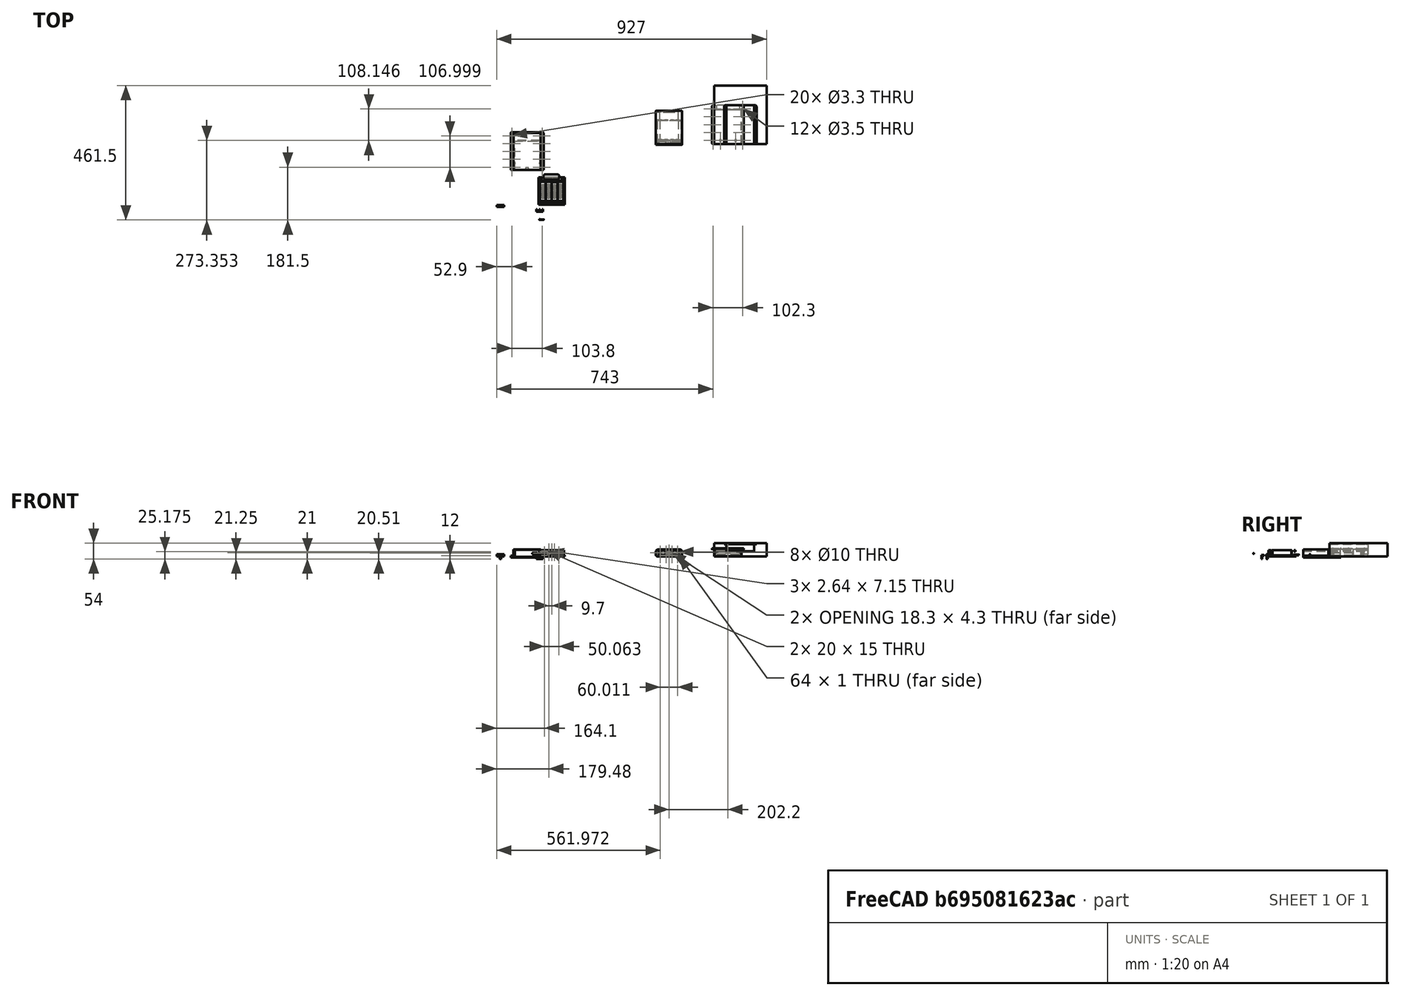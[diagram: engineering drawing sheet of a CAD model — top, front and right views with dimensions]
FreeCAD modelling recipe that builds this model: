
FCSTD DOCUMENT  (FreeCAD 0.21R33771 (Git))
Label: Battery V2
License: All rights reserved
LicenseURL: http://en.wikipedia.org/wiki/All_rights_reserved
objects: Sketcher::SketchObject×80, Part::Extrusion×28, PartDesign::Pocket×22, PartDesign::Fillet×19, App::Part×15, PartDesign::Pad×14, PartDesign::Body×13, PartDesign::Hole×13, App::MeasureDistance×12, Part::Feature×10, PartDesign::FeatureBase×10
note: 277 computed .brp shape members not serialized (recipe doc carries the construction recipe); baked Part::Feature solids carry a one-line shape summary decoded from their .brp

FEATURE [PartDesign::Body] BaseFeature010Body
  Origin = -> Origin117
FEATURE [PartDesign::Body] Body007  label="CELL MOUNT BODY"
  Origin = -> Origin098
FEATURE [PartDesign::Body] Body008  label="BACK BODY"
  Origin = -> Origin100
FEATURE [PartDesign::Body] Body011  label="HANDLE FASTEN PIN BODY"
  Origin = -> Origin106
FEATURE [App::MeasureDistance] Distance019  label="Distance: 3.33780 mm"
  Distance = 3.3378
  P1 = (43.5,-109.3,19.3861)
  P2 = (43.16,-112.62,19.44)
FEATURE [App::MeasureDistance] Distance020  label="Distance: 94.93000 mm"
  Distance = 94.93
  P1 = (84.2,-109.301,22.88)
  P2 = (84.2,-14.3705,22.88)
FEATURE [App::MeasureDistance] Distance021  label="Distance: 84.03434 mm"
  Distance = 84.0343
  P1 = (0.165655,-109.301,22.88)
  P2 = (84.2,-109.301,22.88)
FEATURE [App::MeasureDistance] Distance022  label="Distance: 22.78329 mm"
  Distance = 22.7833
  P1 = (0,-14.3705,22.7833)
  P2 = (0,-14.4,0)
FEATURE [App::MeasureDistance] Distance023  label="Distance: 10.06841 mm"
  Distance = 10.0684
  P1 = (82.0192,-16.37,21.3)
  P2 = (82.2,-26.4368,21.3)
FEATURE [App::MeasureDistance] Distance024  label="Distance: 7.48747 mm"
  Distance = 7.48747
  P1 = (82.0952,-107.281,21.3)
  P2 = (82.1396,-99.794,21.3)
FEATURE [App::MeasureDistance] Distance025  label="Distance: 1.03116 mm"
  Distance = 1.03116
  P1 = (82.2,-95.6714,11.6529)
  P2 = (82.1272,-96.7,11.65)
FEATURE [App::MeasureDistance] Distance026  label="Distance: 0.98878 mm"
  Distance = 0.988782
  P1 = (62.8884,-97.788,21.3)
  P2 = (61.9,-97.7591,21.3)
FEATURE [App::MeasureDistance] Distance027  label="Distance: 3.00017 mm"
  Distance = 3.00017
  P1 = (0,-109.3,3.96765)
  P2 = (-3,-109.3,3.93616)
FEATURE [App::MeasureDistance] Distance028  label="Distance: 90.20000 mm"
  Distance = 90.2
  P1 = (-3,-109.3,0)
  P2 = (87.2,-109.302,0)
FEATURE [App::MeasureDistance] Distance029  label="Distance: 94.80000 mm"
  Distance = 94.8
  P1 = (89.5,2.74181e-07,-2.3)
  P2 = (-5.3,2.74181e-07,-2.3)
FEATURE [App::MeasureDistance] Distance030  label="Distance: 94.92901 mm"
  Distance = 94.929
  P1 = (0,-109.3,22.6426)
  P2 = (0,-14.3705,22.6545)
FEATURE [App::Part] Part027  label="Batt Measurements"
  Group = -> [Distance019,Distance020,Distance021,Distance022,Distance023,Distance024,Distance025,Distance026,Distance027,Distance028,Distance029,Distance030]
  Origin = -> Origin110
FEATURE [Part::Feature] Part__Feature318  label="cell 001"
  Placement = pos=(11.67,-30.7,11.73) rot=(1,0,0;1.5708rad)
  shape: bbox 19.48 x 65 x 19.48 mm, 202 faces (baked)
FEATURE [Part::Feature] Part__Feature319  label="cell 002"
  Placement = pos=(32.21,-30.56,12.09) rot=(1,0,0;1.5708rad)
  shape: bbox 19.48 x 65 x 19.48 mm, 202 faces (baked)
FEATURE [Part::Feature] Part__Feature320  label="cell 003"
  Placement = pos=(52.45,-30.79,11.7) rot=(1,0,0;1.5708rad)
  shape: bbox 19.48 x 65 x 19.48 mm, 202 faces (baked)
FEATURE [Part::Feature] Part__Feature321  label="cell 004"
  Placement = pos=(72.58,-30.46,11.13) rot=(1,0,0;1.5708rad)
  shape: bbox 19.48 x 65 x 19.48 mm, 202 faces (baked)
FEATURE [App::Part] Part022  label="Batt Cells"
  Group = -> [Part__Feature318,Part__Feature319,Part__Feature320,Part__Feature321]
  Origin = -> Origin099
FEATURE [Part::Feature] Part__Feature565  label="sleeve enclosure v2"
  Placement = pos=(-0.1,0,24.3) rot=(0,1,0;3.14159rad)
  shape: bbox 112.8 x 127 x 25.3 mm, 56 faces (baked)
FEATURE [Part::Feature] Part__Feature566  label="sleeve enclosure top plate"
  Placement = pos=(-143.1,1e-15,-1) rot=(0,1,0;3.14159rad)
  shape: bbox 112.8 x 130 x 3 mm, 32 faces (baked)
FEATURE [App::Part] Part043  label="Battery Sleeve"
  Group = -> [Part__Feature565,Part__Feature566]
  Origin = -> Origin199
  Placement = pos=(84,-140.1,-3.2) rot=(0,0,1;0rad)
FEATURE [Sketcher::SketchObject] Sketch080
  FullyConstrained = false
  MapMode = 5
  Support = -> [XY_Plane098]
  sketch-geometry (4):
    g0: LineSegment StartX=0 StartY=-99.794 StartZ=0 EndX=84.2 EndY=-99.794 EndZ=0
    g1: LineSegment StartX=84.2 StartY=-99.794 StartZ=0 EndX=84.2 EndY=-26.494 EndZ=0
    g2: LineSegment StartX=84.2 StartY=-26.494 StartZ=0 EndX=0 EndY=-26.494 EndZ=0
    g3: LineSegment StartX=0 StartY=-26.494 StartZ=0 EndX=0 EndY=-99.794 EndZ=0
  constraints (10):
    c: Coincident(g0,g1)
    c: Coincident(g1,g2)
    c: Coincident(g2,g3)
    c: Coincident(g3,g0)
    c: Horizontal(g0)
    c: Horizontal(g2)
    c: Vertical(g1)
    c: Vertical(g3)
    c: DistanceX(g2,g2) = 84.2
    c: DistanceY(g3,g3) = 73.3
FEATURE [Part::Extrusion] Extrude026  label="CELL MOUNT FLOOR"
  Base = -> Sketch080
  Dir = (0,0,1)
  DirMode = 2
  FaceMakerClass = Part::FaceMakerBullseye
  LengthFwd = 2
  LengthRev = 0
  Solid = true
  Symmetric = false
FEATURE [Sketcher::SketchObject] Sketch081
  FullyConstrained = false
  MapMode = 5
  Placement = pos=(0,0,2) rot=(0,0,1;0rad)
  Support = -> [Extrude026]
  sketch-geometry (12):
    g0: LineSegment StartX=0 StartY=-26.494 StartZ=0 EndX=84.2 EndY=-26.494 EndZ=0
    g1: LineSegment StartX=84.2 StartY=-26.494 StartZ=0 EndX=84.2 EndY=-99.794 EndZ=0
    g2: LineSegment StartX=84.2 StartY=-99.794 StartZ=0 EndX=0 EndY=-99.794 EndZ=0
    g3: LineSegment StartX=0 StartY=-99.794 StartZ=0 EndX=0 EndY=-26.494 EndZ=0
    g4: LineSegment StartX=84.2 StartY=-99.794 StartZ=0 EndX=84.2 EndY=-97.79 EndZ=0
    g5: LineSegment StartX=84.2 StartY=-97.79 StartZ=0 EndX=82.2 EndY=-97.79 EndZ=0
    g6: LineSegment StartX=0 StartY=-26.494 StartZ=0 EndX=0 EndY=-28.49 EndZ=0
    g7: LineSegment StartX=0 StartY=-28.49 StartZ=0 EndX=2 EndY=-28.49 EndZ=0
    g8: LineSegment StartX=2 StartY=-28.49 StartZ=0 EndX=82.2 EndY=-28.49 EndZ=0
    g9: LineSegment StartX=82.2 StartY=-28.49 StartZ=0 EndX=82.2 EndY=-97.79 EndZ=0
    g10: LineSegment StartX=82.2 StartY=-97.79 StartZ=0 EndX=2 EndY=-97.79 EndZ=0
    g11: LineSegment StartX=2 StartY=-97.79 StartZ=0 EndX=2 EndY=-28.49 EndZ=0
  constraints (31):
    c: Coincident(g0,g1)
    c: Coincident(g1,g2)
    c: Coincident(g2,g3)
    c: Coincident(g3,g0)
    c: Horizontal(g0)
    c: Horizontal(g2)
    c: Vertical(g1)
    c: Vertical(g3)
    c: PointOnObject(g0,g-2)
    c: DistanceX(g2,g2) = 84.2
    c: DistanceY(g1,g1) = 73.3
    c: Coincident(g4,g1)
    c: PointOnObject(g4,g1)
    c: Coincident(g5,g4)
    c: Horizontal(g5)
    c: Coincident(g6,g0)
    c: PointOnObject(g6,g3)
    c: Coincident(g7,g6)
    c: Horizontal(g7)
    c: Coincident(g8,g9)
    c: Coincident(g9,g10)
    c: Coincident(g10,g11)
    c: Coincident(g11,g8)
    c: Horizontal(g8)
    c: Horizontal(g10)
    c: Vertical(g9)
    c: Vertical(g11)
    c: Coincident(g8,g7)
    c: Coincident(g9,g5)
    c: DistanceX(g8,g8) = 80.2
    c: DistanceY(g9,g9) = 69.3
FEATURE [Part::Extrusion] Extrude027  label="CELL MOUNT EXT WALLS"
  Base = -> Sketch081
  Dir = (0,0,1)
  DirMode = 2
  FaceMakerClass = Part::FaceMakerBullseye
  LengthFwd = 19.3
  LengthRev = 0
  Solid = true
  Symmetric = false
FEATURE [PartDesign::FeatureBase] BaseFeature012
  BaseFeature = -> Extrude027
FEATURE [Sketcher::SketchObject] Sketch082
  FullyConstrained = false
  MapMode = 5
  Placement = pos=(0,0,2) rot=(0,0,1;0rad)
  Support = -> [Extrude026]
  sketch-geometry (15):
    g0: LineSegment StartX=22.2999 StartY=-28.6 StartZ=0 EndX=41.5999 EndY=-28.6 EndZ=0
    g1: LineSegment StartX=21.2995 StartY=-28.49 StartZ=0 EndX=22.2995 EndY=-28.49 EndZ=0
    g2: LineSegment StartX=22.2995 StartY=-28.49 StartZ=0 EndX=22.2995 EndY=-97.8 EndZ=0
    g3: LineSegment StartX=22.2995 StartY=-97.8 StartZ=0 EndX=21.2995 EndY=-97.8 EndZ=0
    g4: LineSegment StartX=21.2995 StartY=-97.8 StartZ=0 EndX=21.2995 EndY=-28.49 EndZ=0
    g5: LineSegment StartX=41.6 StartY=-28.49 StartZ=0 EndX=42.6 EndY=-28.49 EndZ=0
    g6: LineSegment StartX=42.6 StartY=-28.49 StartZ=0 EndX=42.6 EndY=-97.79 EndZ=0
    g7: LineSegment StartX=42.6 StartY=-97.79 StartZ=0 EndX=41.6 EndY=-97.79 EndZ=0
    g8: LineSegment StartX=41.6 StartY=-97.79 StartZ=0 EndX=41.6 EndY=-28.49 EndZ=0
    g9: LineSegment StartX=42.6 StartY=-28.6021 StartZ=0 EndX=61.9 EndY=-28.6021 EndZ=0
    g10: LineSegment StartX=61.9 StartY=-28.49 StartZ=0 EndX=62.9 EndY=-28.49 EndZ=0
    g11: LineSegment StartX=62.9 StartY=-28.49 StartZ=0 EndX=62.9 EndY=-97.8 EndZ=0
    g12: LineSegment StartX=62.9 StartY=-97.8 StartZ=0 EndX=61.9 EndY=-97.8 EndZ=0
    g13: LineSegment StartX=61.9 StartY=-97.8 StartZ=0 EndX=61.9 EndY=-28.49 EndZ=0
    g14: LineSegment StartX=62.9 StartY=-28.601 StartZ=0 EndX=82.2 EndY=-28.601 EndZ=0
  constraints (38):
    c: Horizontal(g0)
    c: Coincident(g1,g2)
    c: Coincident(g2,g3)
    c: Coincident(g3,g4)
    c: Coincident(g4,g1)
    c: Horizontal(g1)
    c: Horizontal(g3)
    c: Vertical(g2)
    c: Vertical(g4)
    c: Coincident(g5,g6)
    c: Coincident(g6,g7)
    c: Coincident(g7,g8)
    c: Coincident(g8,g5)
    c: Horizontal(g5)
    c: Horizontal(g7)
    c: Vertical(g6)
    c: Vertical(g8)
    c: PointOnObject(g9,g6)
    c: Horizontal(g9)
    c: Coincident(g10,g11)
    c: Coincident(g11,g12)
    c: Coincident(g12,g13)
    c: Coincident(g13,g10)
    c: Horizontal(g10)
    c: Horizontal(g12)
    c: Vertical(g11)
    c: Vertical(g13)
    c: PointOnObject(g14,g11)
    c: Horizontal(g14)
    c: DistanceY(g4,g4) = 69.31
    c: DistanceY(g8,g8) = 69.3
    c: DistanceY(g13,g13) = 69.31
    c: DistanceX(g1,g1) = 1
    c: DistanceX(g0,g0) = 19.3
    c: DistanceX(g9,g9) = 19.3
    c: DistanceX(g5,g5) = 1
    c: DistanceX(g10,g10) = 1
    c: DistanceX(g14,g14) = 19.3
FEATURE [Part::Extrusion] Extrude028  label="CELL DIVIDER WALLS"
  Base = -> Sketch082
  Dir = (0,0,1)
  DirMode = 2
  FaceMakerClass = Part::FaceMakerBullseye
  LengthFwd = 19.3
  LengthRev = 0
  Solid = true
  Symmetric = false
FEATURE [Sketcher::SketchObject] Sketch083
  FullyConstrained = false
  MapMode = 5
  Placement = pos=(0,0,2) rot=(0,0,1;0rad)
  Support = -> [Extrude026]
  sketch-geometry (66):
    g0: LineSegment StartX=2.1 StartY=-28.49 StartZ=0 EndX=2.1 EndY=-29.49 EndZ=0
    g1: LineSegment StartX=2 StartY=-29.5 StartZ=0 EndX=6.5 EndY=-29.5 EndZ=0
    g2: LineSegment StartX=6.5 StartY=-29.5 StartZ=0 EndX=6.5 EndY=-30.5 EndZ=0
    g3: LineSegment StartX=6.5 StartY=-30.5 StartZ=0 EndX=2 EndY=-30.5 EndZ=0
    g4: LineSegment StartX=2 StartY=-30.5 StartZ=0 EndX=2 EndY=-29.5 EndZ=0
    g5: LineSegment StartX=21.3 StartY=-29.49 StartZ=0 EndX=16.8 EndY=-29.49 EndZ=0
    g6: LineSegment StartX=16.8 StartY=-29.49 StartZ=0 EndX=16.8 EndY=-30.49 EndZ=0
    g7: LineSegment StartX=16.8 StartY=-30.49 StartZ=0 EndX=21.3 EndY=-30.49 EndZ=0
    g8: LineSegment StartX=21.3 StartY=-30.49 StartZ=0 EndX=21.3 EndY=-29.49 EndZ=0
    g9: LineSegment StartX=22.3 StartY=-30.49 StartZ=0 EndX=26.8 EndY=-30.49 EndZ=0
    g10: LineSegment StartX=26.8 StartY=-30.49 StartZ=0 EndX=26.8 EndY=-29.49 EndZ=0
    g11: LineSegment StartX=26.8 StartY=-29.49 StartZ=0 EndX=22.3 EndY=-29.49 EndZ=0
    g12: LineSegment StartX=22.3 StartY=-29.49 StartZ=0 EndX=22.3 EndY=-30.49 EndZ=0
    g13: LineSegment StartX=41.6 StartY=-29.5 StartZ=0 EndX=37.1 EndY=-29.5 EndZ=0
    g14: LineSegment StartX=37.1 StartY=-29.5 StartZ=0 EndX=37.1 EndY=-30.5 EndZ=0
    g15: LineSegment StartX=37.1 StartY=-30.5 StartZ=0 EndX=41.6 EndY=-30.5 EndZ=0
    g16: LineSegment StartX=41.6 StartY=-30.5 StartZ=0 EndX=41.6 EndY=-29.5 EndZ=0
    g17: LineSegment StartX=42.6 StartY=-29.5 StartZ=0 EndX=47.1 EndY=-29.5 EndZ=0
    g18: LineSegment StartX=47.1 StartY=-29.5 StartZ=0 EndX=47.1 EndY=-30.5 EndZ=0
    g19: LineSegment StartX=47.1 StartY=-30.5 StartZ=0 EndX=42.6 EndY=-30.5 EndZ=0
    g20: LineSegment StartX=42.6 StartY=-30.5 StartZ=0 EndX=42.6 EndY=-29.5 EndZ=0
    g21: LineSegment StartX=61.9 StartY=-29.5 StartZ=0 EndX=57.4 EndY=-29.5 EndZ=0
    g22: LineSegment StartX=57.4 StartY=-29.5 StartZ=0 EndX=57.4 EndY=-30.5 EndZ=0
    g23: LineSegment StartX=57.4 StartY=-30.5 StartZ=0 EndX=61.9 EndY=-30.5 EndZ=0
    g24: LineSegment StartX=61.9 StartY=-30.5 StartZ=0 EndX=61.9 EndY=-29.5 EndZ=0
    g25: LineSegment StartX=62.9 StartY=-29.5 StartZ=0 EndX=67.4 EndY=-29.5 EndZ=0
    g26: LineSegment StartX=67.4 StartY=-29.5 StartZ=0 EndX=67.4 EndY=-30.5 EndZ=0
    g27: LineSegment StartX=67.4 StartY=-30.5 StartZ=0 EndX=62.9 EndY=-30.5 EndZ=0
    g28: LineSegment StartX=62.9 StartY=-30.5 StartZ=0 EndX=62.9 EndY=-29.5 EndZ=0
    g29: LineSegment StartX=82.2 StartY=-29.5 StartZ=0 EndX=77.7 EndY=-29.5 EndZ=0
    g30: LineSegment StartX=77.7 StartY=-29.5 StartZ=0 EndX=77.7 EndY=-30.5 EndZ=0
    g31: LineSegment StartX=77.7 StartY=-30.5 StartZ=0 EndX=82.2 EndY=-30.5 EndZ=0
    g32: LineSegment StartX=82.2 StartY=-30.5 StartZ=0 EndX=82.2 EndY=-29.5 EndZ=0
    g33: LineSegment StartX=2.1 StartY=-97.79 StartZ=0 EndX=2.1 EndY=-96.7 EndZ=0
    g34: LineSegment StartX=2 StartY=-96.7 StartZ=0 EndX=6.5 EndY=-96.7 EndZ=0
    g35: LineSegment StartX=6.5 StartY=-96.7 StartZ=0 EndX=6.5 EndY=-95.7 EndZ=0
    g36: LineSegment StartX=6.5 StartY=-95.7 StartZ=0 EndX=2 EndY=-95.7 EndZ=0
    g37: LineSegment StartX=2 StartY=-95.7 StartZ=0 EndX=2 EndY=-96.7 EndZ=0
    g38: LineSegment StartX=21.3 StartY=-95.7 StartZ=0 EndX=16.8 EndY=-95.7 EndZ=0
    g39: LineSegment StartX=16.8 StartY=-95.7 StartZ=0 EndX=16.8 EndY=-96.7 EndZ=0
    g40: LineSegment StartX=16.8 StartY=-96.7 StartZ=0 EndX=21.3 EndY=-96.7 EndZ=0
    g41: LineSegment StartX=21.3 StartY=-96.7 StartZ=0 EndX=21.3 EndY=-95.7 EndZ=0
    g42: LineSegment StartX=22.3 StartY=-96.7 StartZ=0 EndX=26.8 EndY=-96.7 EndZ=0
    g43: LineSegment StartX=26.8 StartY=-96.7 StartZ=0 EndX=26.8 EndY=-95.7 EndZ=0
    g44: LineSegment StartX=26.8 StartY=-95.7 StartZ=0 EndX=22.3 EndY=-95.7 EndZ=0
    g45: LineSegment StartX=22.3 StartY=-95.7 StartZ=0 EndX=22.3 EndY=-96.7 EndZ=0
    g46: LineSegment StartX=41.6 StartY=-95.7 StartZ=0 EndX=37.1 EndY=-95.7 EndZ=0
    g47: LineSegment StartX=37.1 StartY=-95.7 StartZ=0 EndX=37.1 EndY=-96.7 EndZ=0
    g48: LineSegment StartX=37.1 StartY=-96.7 StartZ=0 EndX=41.6 EndY=-96.7 EndZ=0
    g49: LineSegment StartX=41.6 StartY=-96.7 StartZ=0 EndX=41.6 EndY=-95.7 EndZ=0
    g50: LineSegment StartX=42.6 StartY=-96.7 StartZ=0 EndX=47.1 EndY=-96.7 EndZ=0
    g51: LineSegment StartX=47.1 StartY=-96.7 StartZ=0 EndX=47.1 EndY=-95.7 EndZ=0
    g52: LineSegment StartX=47.1 StartY=-95.7 StartZ=0 EndX=42.6 EndY=-95.7 EndZ=0
    g53: LineSegment StartX=42.6 StartY=-95.7 StartZ=0 EndX=42.6 EndY=-96.7 EndZ=0
    g54: LineSegment StartX=61.9 StartY=-95.7 StartZ=0 EndX=57.4 EndY=-95.7 EndZ=0
    g55: LineSegment StartX=57.4 StartY=-95.7 StartZ=0 EndX=57.4 EndY=-96.7 EndZ=0
    g56: LineSegment StartX=57.4 StartY=-96.7 StartZ=0 EndX=61.9 EndY=-96.7 EndZ=0
    g57: LineSegment StartX=61.9 StartY=-96.7 StartZ=0 EndX=61.9 EndY=-95.7 EndZ=0
    g58: LineSegment StartX=62.9 StartY=-95.7 StartZ=0 EndX=67.4 EndY=-95.7 EndZ=0
    g59: LineSegment StartX=67.4 StartY=-95.7 StartZ=0 EndX=67.4 EndY=-96.7 EndZ=0
    g60: LineSegment StartX=67.4 StartY=-96.7 StartZ=0 EndX=62.9 EndY=-96.7 EndZ=0
    g61: LineSegment StartX=62.9 StartY=-96.7 StartZ=0 EndX=62.9 EndY=-95.7 EndZ=0
    g62: LineSegment StartX=82.2 StartY=-95.7 StartZ=0 EndX=77.7 EndY=-95.7 EndZ=0
    g63: LineSegment StartX=77.7 StartY=-95.7 StartZ=0 EndX=77.7 EndY=-96.7 EndZ=0
    g64: LineSegment StartX=77.7 StartY=-96.7 StartZ=0 EndX=82.2 EndY=-96.7 EndZ=0
    g65: LineSegment StartX=82.2 StartY=-96.7 StartZ=0 EndX=82.2 EndY=-95.7 EndZ=0
  constraints (162):
    c: Vertical(g0)
    c: Coincident(g1,g2)
    c: Coincident(g2,g3)
    c: Coincident(g3,g4)
    c: Coincident(g4,g1)
    c: Horizontal(g1)
    c: Horizontal(g3)
    c: Vertical(g2)
    c: Vertical(g4)
    c: Coincident(g5,g6)
    c: Coincident(g6,g7)
    c: Coincident(g7,g8)
    c: Coincident(g8,g5)
    c: Horizontal(g5)
    c: Horizontal(g7)
    c: Vertical(g6)
    c: Vertical(g8)
    c: DistanceX(g1,g1) = 4.5
    c: DistanceX(g5,g5) = 4.5
    c: DistanceY(g2,g2) = 1
    c: DistanceY(g6,g6) = 1
    c: Coincident(g9,g10)
    c: Coincident(g10,g11)
    c: Coincident(g11,g12)
    c: Coincident(g12,g9)
    c: Horizontal(g9)
    c: Horizontal(g11)
    c: Vertical(g10)
    c: Vertical(g12)
    c: Coincident(g13,g14)
    c: Coincident(g14,g15)
    c: Coincident(g15,g16)
    c: Coincident(g16,g13)
    c: Horizontal(g13)
    c: Horizontal(g15)
    c: Vertical(g14)
    c: Vertical(g16)
    c: DistanceX(g13,g13) = 4.5
    c: DistanceX(g11,g11) = 4.5
    c: DistanceY(g10,g10) = 1
    c: DistanceY(g14,g14) = 1
    c: Coincident(g17,g18)
    c: Coincident(g18,g19)
    c: Coincident(g19,g20)
    c: Coincident(g20,g17)
    c: Horizontal(g17)
    c: Horizontal(g19)
    c: Vertical(g18)
    c: Vertical(g20)
    c: Coincident(g21,g22)
    c: Coincident(g22,g23)
    c: Coincident(g23,g24)
    c: Coincident(g24,g21)
    c: Horizontal(g21)
    c: Horizontal(g23)
    c: Vertical(g22)
    c: Vertical(g24)
    c: DistanceX(g17,g17) = 4.5
    c: DistanceY(g18,g18) = 1
    c: DistanceX(g21,g21) = 4.5
    c: DistanceY(g22,g22) = 1
    c: Coincident(g25,g26)
    c: Coincident(g26,g27)
    c: Coincident(g27,g28)
    c: Coincident(g28,g25)
    c: Horizontal(g25)
    c: Horizontal(g27)
    c: Vertical(g26)
    c: Vertical(g28)
    c: Coincident(g29,g30)
    c: Coincident(g30,g31)
    c: Coincident(g31,g32)
    c: Coincident(g32,g29)
    c: Horizontal(g29)
    c: Horizontal(g31)
    c: Vertical(g30)
    c: Vertical(g32)
    c: DistanceX(g29,g29) = 4.5
    c: DistanceX(g25,g25) = 4.5
    c: DistanceY(g26,g26) = 1
    c: DistanceY(g30,g30) = 1
    c: Vertical(g33)
    c: Coincident(g34,g35)
    c: Coincident(g35,g36)
    c: Coincident(g36,g37)
    c: Coincident(g37,g34)
    c: Horizontal(g34)
    c: Horizontal(g36)
    c: Vertical(g35)
    c: Vertical(g37)
    c: Coincident(g38,g39)
    c: Coincident(g39,g40)
    c: Coincident(g40,g41)
    c: Coincident(g41,g38)
    c: Horizontal(g38)
    c: Horizontal(g40)
    c: Vertical(g39)
    c: Vertical(g41)
    c: DistanceY(g39,g39) = 1
    c: DistanceY(g35,g35) = 1
    c: DistanceX(g36,g36) = 4.5
    c: DistanceX(g38,g38) = 4.5
    c: Coincident(g42,g43)
    c: Coincident(g43,g44)
    c: Coincident(g44,g45)
    c: Coincident(g45,g42)
    c: Horizontal(g42)
    c: Horizontal(g44)
    c: Vertical(g43)
    c: Vertical(g45)
    c: Coincident(g46,g47)
    c: Coincident(g47,g48)
    c: Coincident(g48,g49)
    c: Coincident(g49,g46)
    c: Horizontal(g46)
    c: Horizontal(g48)
    c: Vertical(g47)
    c: Vertical(g49)
    c: DistanceX(g46,g46) = 4.5
    c: DistanceX(g44,g44) = 4.5
    c: DistanceY(g43,g43) = 1
    c: DistanceY(g47,g47) = 1
    c: Coincident(g50,g51)
    c: Coincident(g51,g52)
    c: Coincident(g52,g53)
    c: Coincident(g53,g50)
    c: Horizontal(g50)
    c: Horizontal(g52)
    c: Vertical(g51)
    c: Vertical(g53)
    c: DistanceY(g51,g51) = 1
    c: DistanceX(g52,g52) = 4.5
    c: Coincident(g54,g55)
    c: Coincident(g55,g56)
    c: Coincident(g56,g57)
    c: Coincident(g57,g54)
    c: Horizontal(g54)
    c: Horizontal(g56)
    c: Vertical(g55)
    c: Vertical(g57)
    c: DistanceX(g54,g54) = 4.5
    c: DistanceY(g55,g55) = 1
    c: Coincident(g58,g59)
    c: Coincident(g59,g60)
    c: Coincident(g60,g61)
    c: Coincident(g61,g58)
    c: Horizontal(g58)
    c: Horizontal(g60)
    c: Vertical(g59)
    c: Vertical(g61)
    c: DistanceY(g59,g59) = 1
    c: DistanceX(g60,g60) = 4.5
    c: Coincident(g62,g63)
    c: Coincident(g63,g64)
    c: Coincident(g64,g65)
    c: Coincident(g65,g62)
    c: Horizontal(g62)
    c: Horizontal(g64)
    c: Vertical(g63)
    c: Vertical(g65)
    c: DistanceY(g63,g63) = 1
    c: DistanceX(g62,g62) = 4.5
FEATURE [Part::Extrusion] Extrude029  label="CELL ENDS SPRING HOLDERS"
  Base = -> Sketch083
  Dir = (0,0,1)
  DirMode = 2
  FaceMakerClass = Part::FaceMakerBullseye
  LengthFwd = 9.65
  LengthRev = 0
  Solid = true
  Symmetric = false
FEATURE [Sketcher::SketchObject] Sketch084
  FullyConstrained = false
  MapMode = 5
  Support = -> [XY_Plane098]
  sketch-geometry (4):
    g0: LineSegment StartX=0 StartY=-26.49 StartZ=0 EndX=84.2 EndY=-26.49 EndZ=0
    g1: LineSegment StartX=84.2 StartY=-26.49 StartZ=0 EndX=84.2 EndY=-14.4 EndZ=0
    g2: LineSegment StartX=84.2 StartY=-14.4 StartZ=0 EndX=0 EndY=-14.4 EndZ=0
    g3: LineSegment StartX=0 StartY=-14.4 StartZ=0 EndX=0 EndY=-26.49 EndZ=0
  constraints (11):
    c: Coincident(g0,g1)
    c: Coincident(g1,g2)
    c: Coincident(g2,g3)
    c: Coincident(g3,g0)
    c: Horizontal(g0)
    c: Horizontal(g2)
    c: Vertical(g1)
    c: Vertical(g3)
    c: PointOnObject(g0,g-2)
    c: DistanceX(g2,g2) = 84.2
    c: DistanceY(g1,g1) = 12.09
FEATURE [Part::Extrusion] Extrude030  label="BACK FLOOR"
  Base = -> Sketch084
  Dir = (0,0,1)
  DirMode = 2
  FaceMakerClass = Part::FaceMakerBullseye
  LengthFwd = 2
  LengthRev = 0
  Solid = true
  Symmetric = false
FEATURE [Sketcher::SketchObject] Sketch085
  FullyConstrained = false
  MapMode = 5
  Placement = pos=(0,0,2) rot=(0,0,1;0rad)
  Support = -> [Extrude030]
  sketch-geometry (8):
    g0: LineSegment StartX=0 StartY=-26.4942 StartZ=0 EndX=84.2 EndY=-26.4942 EndZ=0
    g1: LineSegment StartX=84.2 StartY=-26.4942 StartZ=0 EndX=84.2 EndY=-14.4 EndZ=0
    g2: LineSegment StartX=84.2 StartY=-14.4 StartZ=0 EndX=0 EndY=-14.4 EndZ=0
    g3: LineSegment StartX=0 StartY=-14.4 StartZ=0 EndX=0 EndY=-26.4942 EndZ=0
    g4: LineSegment StartX=82.2 StartY=-26.4942 StartZ=0 EndX=2 EndY=-26.4942 EndZ=0
    g5: LineSegment StartX=2 StartY=-26.4942 StartZ=0 EndX=2 EndY=-16.37 EndZ=0
    g6: LineSegment StartX=2 StartY=-16.37 StartZ=0 EndX=82.2 EndY=-16.37 EndZ=0
    g7: LineSegment StartX=82.2 StartY=-16.37 StartZ=0 EndX=82.2 EndY=-26.4942 EndZ=0
  constraints (22):
    c: Coincident(g0,g1)
    c: Coincident(g1,g2)
    c: Coincident(g2,g3)
    c: Coincident(g3,g0)
    c: Horizontal(g0)
    c: Horizontal(g2)
    c: Vertical(g1)
    c: Vertical(g3)
    c: PointOnObject(g0,g-2)
    c: Coincident(g4,g5)
    c: Coincident(g5,g6)
    c: Coincident(g6,g7)
    c: Coincident(g7,g4)
    c: Horizontal(g4)
    c: Horizontal(g6)
    c: Vertical(g5)
    c: Vertical(g7)
    c: PointOnObject(g4,g0)
    c: DistanceX(g6,g6) = 80.2
    c: DistanceX(g2,g2) = 84.2
    c: DistanceY(g5,g5) = 10.1242
    c: DistanceY(g3,g3) = 12.0942
FEATURE [Part::Extrusion] Extrude005  label="Extrude062"
  Base = -> Sketch085
  Dir = (0,0,1)
  DirMode = 2
  FaceMakerClass = Part::FaceMakerBullseye
  LengthFwd = 19.3
  LengthRev = 0
  Solid = true
  Symmetric = false
FEATURE [PartDesign::FeatureBase] BaseFeature006
  BaseFeature = -> Extrude005
FEATURE [Sketcher::SketchObject] Sketch086
  FullyConstrained = false
  MapMode = 5
  Placement = pos=(0,-14.4,0) rot=(0,0.707107,0.707107;3.14159rad)
  Support = -> [BaseFeature006]
  sketch-geometry (4):
    g0: LineSegment StartX=-7 StartY=10 StartZ=0 EndX=-24.64 EndY=10 EndZ=0
    g1: LineSegment StartX=-24.64 StartY=10 StartZ=0 EndX=-24.64 EndY=14 EndZ=0
    g2: LineSegment StartX=-24.64 StartY=14 StartZ=0 EndX=-7 EndY=14 EndZ=0
    g3: LineSegment StartX=-7 StartY=14 StartZ=0 EndX=-7 EndY=10 EndZ=0
  constraints (10):
    c: Coincident(g0,g1)
    c: Coincident(g1,g2)
    c: Coincident(g2,g3)
    c: Coincident(g3,g0)
    c: Horizontal(g0)
    c: Horizontal(g2)
    c: Vertical(g1)
    c: Vertical(g3)
    c: DistanceX(g2,g2) = 17.64
    c: DistanceY(g1,g1) = 4
FEATURE [PartDesign::Pocket] Pocket017  label="BACK WALL"
  Direction = (0,-1,2e-16)
  Length = 2
  Length2 = 5
  Profile = -> Sketch086
  ReferenceAxis = -> Sketch086 [N_Axis]
  Type = 0
FEATURE [Sketcher::SketchObject] Sketch087
  FullyConstrained = false
  MapMode = 5
  Support = -> [XY_Plane102]
  sketch-geometry (4):
    g0: LineSegment StartX=-140 StartY=-110 StartZ=0 EndX=-128 EndY=-110 EndZ=0
    g1: LineSegment StartX=-128 StartY=-110 StartZ=0 EndX=-128 EndY=-117 EndZ=0
    g2: LineSegment StartX=-128 StartY=-117 StartZ=0 EndX=-140 EndY=-117 EndZ=0
    g3: LineSegment StartX=-140 StartY=-117 StartZ=0 EndX=-140 EndY=-110 EndZ=0
  constraints (10):
    c: Coincident(g0,g1)
    c: Coincident(g1,g2)
    c: Coincident(g2,g3)
    c: Coincident(g3,g0)
    c: Horizontal(g0)
    c: Horizontal(g2)
    c: Vertical(g1)
    c: Vertical(g3)
    c: DistanceX(g0,g0) = 12
    c: DistanceY(g3,g3) = 7
FEATURE [Part::Extrusion] Extrude007
  Base = -> Sketch087
  Dir = (0,0,1)
  DirMode = 2
  FaceMakerClass = Part::FaceMakerBullseye
  LengthFwd = 7
  LengthRev = 0
  Solid = true
  Symmetric = false
FEATURE [PartDesign::FeatureBase] BaseFeature007
  BaseFeature = -> Extrude007
FEATURE [Sketcher::SketchObject] Sketch012
  FullyConstrained = false
  MapMode = 5
  Placement = pos=(0,0,7) rot=(0,0,1;0rad)
  Support = -> [Extrude007]
  sketch-geometry (4):
    g0: LineSegment StartX=-139 StartY=-111 StartZ=0 EndX=-129 EndY=-111 EndZ=0
    g1: LineSegment StartX=-129 StartY=-111 StartZ=0 EndX=-129 EndY=-116 EndZ=0
    g2: LineSegment StartX=-129 StartY=-116 StartZ=0 EndX=-139 EndY=-116 EndZ=0
    g3: LineSegment StartX=-139 StartY=-116 StartZ=0 EndX=-139 EndY=-111 EndZ=0
  constraints (10):
    c: Coincident(g0,g1)
    c: Coincident(g1,g2)
    c: Coincident(g2,g3)
    c: Coincident(g3,g0)
    c: Horizontal(g0)
    c: Horizontal(g2)
    c: Vertical(g1)
    c: Vertical(g3)
    c: DistanceY(g3,g3) = 5
    c: DistanceX(g0,g0) = 10
FEATURE [Sketcher::SketchObject] Sketch088
  FullyConstrained = false
  MapMode = 5
  Placement = pos=(0,-117,0) rot=(1,0,0;1.5708rad)
  Support = -> [Extrude007]
  sketch-geometry (4):
    g0: LineSegment StartX=-135 StartY=2 StartZ=0 EndX=-133 EndY=2 EndZ=0
    g1: LineSegment StartX=-133 StartY=2 StartZ=0 EndX=-133 EndY=5 EndZ=0
    g2: LineSegment StartX=-133 StartY=5 StartZ=0 EndX=-135 EndY=5 EndZ=0
    g3: LineSegment StartX=-135 StartY=5 StartZ=0 EndX=-135 EndY=2 EndZ=0
  constraints (10):
    c: Coincident(g0,g1)
    c: Coincident(g1,g2)
    c: Coincident(g2,g3)
    c: Coincident(g3,g0)
    c: Horizontal(g0)
    c: Horizontal(g2)
    c: Vertical(g1)
    c: Vertical(g3)
    c: DistanceX(g2,g2) = 2
    c: DistanceY(g3,g3) = 3
FEATURE [PartDesign::Pocket] Pocket018
  Direction = (0,1,-2e-16)
  Length = 3.5
  Length2 = 5
  Profile = -> Sketch088
  ReferenceAxis = -> Sketch088 [N_Axis]
  Type = 0
FEATURE [PartDesign::FeatureBase] BaseFeature008
  BaseFeature = -> Pocket018
FEATURE [Sketcher::SketchObject] Sketch089
  FullyConstrained = false
  MapMode = 5
  Placement = pos=(-128,0,0) rot=(0.57735,0.57735,0.57735;2.0944rad)
  Support = -> [Pocket018]
  sketch-geometry (1):
    g0: Circle CenterX=-115.25 CenterY=3.5 CenterZ=0 NormalX=0 NormalY=0 NormalZ=1 AngleXU=0 Radius=0.75
  constraints (1):
    c: Diameter(g0) = 1.5
FEATURE [PartDesign::Hole] Hole018  label="MAIN LOCKING HANDLE MNT"
  CustomThreadClearance = 0
  Depth = 12
  DepthType = 0
  Diameter = 1.5
  DrillForDepth = false
  DrillPoint = 1
  DrillPointAngle = 118
  HoleCutCountersinkAngle = 90
  HoleCutCustomValues = false
  HoleCutDepth = 0
  HoleCutDiameter = 6.1
  HoleCutType = 0
  ModelThread = false
  Profile = -> Sketch089
  Tapered = false
  TaperedAngle = 90
  ThreadClass = 0
  ThreadDepth = 12
  ThreadDepthType = 0
  ThreadDirection = 0
  ThreadFit = 0
  ThreadSize = 0
  ThreadType = 0
  Threaded = false
  UseCustomThreadClearance = false
FEATURE [Sketcher::SketchObject] Sketch090
  FullyConstrained = false
  MapMode = 5
  Placement = pos=(0,0,0) rot=(0.57735,0.57735,0.57735;2.0944rad)
  Support = -> [YZ_Plane104]
  sketch-geometry (17):
    g0: LineSegment StartX=-128 StartY=5 StartZ=0 EndX=-130 EndY=5 EndZ=0
    g1: LineSegment StartX=-130 StartY=5 StartZ=0 EndX=-130.3 EndY=5 EndZ=0
    g2: LineSegment StartX=-130.3 StartY=5 StartZ=0 EndX=-133.3 EndY=5 EndZ=0
    g3: LineSegment StartX=-133.3 StartY=5 StartZ=0 EndX=-133.3 EndY=3 EndZ=0
    g4: LineSegment StartX=-133.3 StartY=3 StartZ=0 EndX=-131.8 EndY=3 EndZ=0
    g5: LineSegment StartX=-131.8 StartY=3 StartZ=0 EndX=-131.8 EndY=-7 EndZ=0
    g6: LineSegment StartX=-131.8 StartY=-7 StartZ=0 EndX=-133.3 EndY=-7 EndZ=0
    g7: LineSegment StartX=-133.3 StartY=-7 StartZ=0 EndX=-133.3 EndY=-9 EndZ=0
    g8: LineSegment StartX=-133.3 StartY=-9 StartZ=0 EndX=-130.3 EndY=-9 EndZ=0
    g9: LineSegment StartX=-128 StartY=5 StartZ=0 EndX=-127.7 EndY=5 EndZ=0
    g10: LineSegment StartX=-127.7 StartY=5 StartZ=0 EndX=-124.2 EndY=5 EndZ=0
    g11: LineSegment StartX=-124.2 StartY=5 StartZ=0 EndX=-124.2 EndY=2 EndZ=0
    g12: LineSegment StartX=-124.2 StartY=2 StartZ=0 EndX=-127.7 EndY=2 EndZ=0
    g13: LineSegment StartX=-127.7 StartY=2 StartZ=0 EndX=-128 EndY=2 EndZ=0
    g14: LineSegment StartX=-128 StartY=2 StartZ=0 EndX=-130 EndY=2 EndZ=0
    g15: LineSegment StartX=-130 StartY=2 StartZ=0 EndX=-130.3 EndY=2 EndZ=0
    g16: LineSegment StartX=-130.3 StartY=2 StartZ=0 EndX=-130.3 EndY=-9 EndZ=0
  constraints (49):
    c: Horizontal(g0)
    c: Coincident(g0,g1)
    c: Horizontal(g1)
    c: Coincident(g1,g2)
    c: Horizontal(g2)
    c: Coincident(g2,g3)
    c: Vertical(g3)
    c: Coincident(g3,g4)
    c: Horizontal(g4)
    c: Coincident(g4,g5)
    c: Vertical(g5)
    c: Coincident(g5,g6)
    c: Horizontal(g6)
    c: Coincident(g6,g7)
    c: Vertical(g7)
    c: Coincident(g7,g8)
    c: Horizontal(g8)
    c: DistanceY(g5,g5) = 10
    c: DistanceY(g3,g3) = 2
    c: DistanceX(g4,g4) = 1.5
    c: DistanceX(g2,g2) = 3
    c: DistanceX(g1,g1) = 0.3
    c: DistanceX(g0,g0) = 2
    c: DistanceX(g6,g6) = 1.5
    c: Coincident(g9,g0)
    c: Horizontal(g9)
    c: Coincident(g9,g10)
    c: Horizontal(g10)
    c: Coincident(g10,g11)
    c: Vertical(g11)
    c: Coincident(g11,g12)
    c: Horizontal(g12)
    c: Coincident(g12,g13)
    c: Horizontal(g13)
    c: Coincident(g13,g14)
    c: Horizontal(g14)
    c: Coincident(g15,g14)
    c: Horizontal(g15)
    c: Coincident(g15,g16)
    c: Coincident(g16,g8)
    c: Vertical(g16)
    c: DistanceY(g7,g7) = 2
    c: DistanceY(g16,g16) = 11
    c: DistanceX(g8,g8) = 3
    c: DistanceX(g15,g15) = 0.3
    c: DistanceX(g14,g14) = 2
    c: DistanceX(g13,g13) = 0.3
    c: DistanceX(g12,g12) = 3.5
    c: DistanceX(g10,g10) = 3.5
FEATURE [Part::Extrusion] Extrude041  label="Extrude071"
  Base = -> Sketch090
  Dir = (1,-1e-16,1e-16)
  DirMode = 2
  FaceMakerClass = Part::FaceMakerBullseye
  LengthFwd = 2
  LengthRev = 0
  Solid = true
  Symmetric = false
FEATURE [Sketcher::SketchObject] Sketch091
  FullyConstrained = false
  MapMode = 5
  Placement = pos=(0,0,0) rot=(0.57735,0.57735,0.57735;2.0944rad)
  Support = -> [YZ_Plane106]
  sketch-geometry (1):
    g0: Circle CenterX=-160 CenterY=10 CenterZ=0 NormalX=0 NormalY=0 NormalZ=1 AngleXU=0 Radius=1.5
  constraints (1):
    c: Diameter(g0) = 3
FEATURE [Part::Extrusion] Extrude011  label="PIN BASE"
  Base = -> Sketch091
  Dir = (1,-1e-16,1e-16)
  DirMode = 2
  FaceMakerClass = Part::FaceMakerBullseye
  LengthFwd = 1.5
  LengthRev = 0
  Solid = true
  Symmetric = false
FEATURE [Sketcher::SketchObject] Sketch092
  FullyConstrained = false
  MapMode = 5
  Placement = pos=(1.5,-3e-16,3e-16) rot=(0.57735,0.57735,0.57735;2.0944rad)
  Support = -> [Extrude011]
  sketch-geometry (1):
    g0: Circle CenterX=-160 CenterY=10 CenterZ=0 NormalX=0 NormalY=0 NormalZ=1 AngleXU=0 Radius=0.74
  constraints (1):
    c: Diameter(g0) = 1.48
FEATURE [Part::Extrusion] Extrude012  label="PIN LENGTH"
  Base = -> Sketch092
  Dir = (1,-2e-16,2e-16)
  DirMode = 2
  FaceMakerClass = Part::FaceMakerBullseye
  LengthFwd = 13.5
  LengthRev = 0
  Solid = true
  Symmetric = false
FEATURE [App::Part] Part025  label="handle to mechanism pin"
  Group = -> [Body011,Sketch091,Extrude011,Sketch092,Extrude012]
  Origin = -> Origin105
  Placement = pos=(34.67,54.77,7.74) rot=(0,0,1;0rad)
FEATURE [Sketcher::SketchObject] Sketch093
  FullyConstrained = false
  MapMode = 5
  Support = -> [XY_Plane107]
  sketch-geometry (4):
    g0: LineSegment StartX=0 StartY=-99.794 StartZ=0 EndX=84.2 EndY=-99.794 EndZ=0
    g1: LineSegment StartX=84.2 StartY=-99.794 StartZ=0 EndX=84.2 EndY=-109.304 EndZ=0
    g2: LineSegment StartX=84.2 StartY=-109.304 StartZ=0 EndX=0 EndY=-109.304 EndZ=0
    g3: LineSegment StartX=0 StartY=-109.304 StartZ=0 EndX=0 EndY=-99.794 EndZ=0
  constraints (11):
    c: Coincident(g0,g1)
    c: Coincident(g1,g2)
    c: Coincident(g2,g3)
    c: Coincident(g3,g0)
    c: Horizontal(g0)
    c: Horizontal(g2)
    c: Vertical(g1)
    c: Vertical(g3)
    c: PointOnObject(g0,g-2)
    c: DistanceX(g2,g2) = 84.2
    c: DistanceY(g1,g1) = 9.51
FEATURE [Part::Extrusion] Extrude031  label="Extrude063"
  Base = -> Sketch093
  Dir = (0,0,1)
  DirMode = 2
  FaceMakerClass = Part::FaceMakerBullseye
  LengthFwd = 2
  LengthRev = 0
  Solid = true
  Symmetric = false
FEATURE [PartDesign::FeatureBase] BaseFeature009  label="FRONT FLOOR"
  BaseFeature = -> Extrude031
FEATURE [Sketcher::SketchObject] Sketch094
  FullyConstrained = false
  MapMode = 5
  Placement = pos=(0,0,2) rot=(0,0,1;0rad)
  Support = -> [Extrude031]
  sketch-geometry (8):
    g0: LineSegment StartX=0 StartY=-99.8 StartZ=0 EndX=0 EndY=-109.3 EndZ=0
    g1: LineSegment StartX=0 StartY=-109.3 StartZ=0 EndX=84.2 EndY=-109.3 EndZ=0
    g2: LineSegment StartX=84.2 StartY=-109.3 StartZ=0 EndX=84.2 EndY=-99.79 EndZ=0
    g3: LineSegment StartX=84.2 StartY=-99.79 StartZ=0 EndX=82.2 EndY=-99.79 EndZ=0
    g4: LineSegment StartX=82.2 StartY=-99.79 StartZ=0 EndX=82.2 EndY=-107.3 EndZ=0
    g5: LineSegment StartX=82.2 StartY=-107.3 StartZ=0 EndX=2 EndY=-107.3 EndZ=0
    g6: LineSegment StartX=2 StartY=-107.3 StartZ=0 EndX=2 EndY=-99.8 EndZ=0
    g7: LineSegment StartX=2 StartY=-99.8 StartZ=0 EndX=0 EndY=-99.8 EndZ=0
  constraints (23):
    c: PointOnObject(g0,g-2)
    c: PointOnObject(g0,g-2)
    c: Coincident(g0,g1)
    c: Horizontal(g1)
    c: Coincident(g1,g2)
    c: Vertical(g2)
    c: Coincident(g2,g3)
    c: Horizontal(g3)
    c: Coincident(g3,g4)
    c: Vertical(g4)
    c: Coincident(g4,g5)
    c: Horizontal(g5)
    c: Coincident(g5,g6)
    c: Vertical(g6)
    c: Coincident(g6,g7)
    c: Coincident(g7,g0)
    c: Horizontal(g7)
    c: DistanceX(g7,g7) = 2
    c: DistanceX(g1,g1) = 84.2
    c: DistanceX(g5,g5) = 80.2
    c: DistanceY(g2,g2) = 9.51
    c: DistanceY(g4,g4) = 7.51
    c: DistanceY(g6,g6) = 7.5
FEATURE [Part::Extrusion] Extrude032  label="FRONT WALL"
  Base = -> Sketch094
  Dir = (0,0,1)
  DirMode = 2
  FaceMakerClass = Part::FaceMakerBullseye
  LengthFwd = 19.3
  LengthRev = 0
  Solid = true
  Symmetric = false
FEATURE [PartDesign::FeatureBase] BaseFeature011
  BaseFeature = -> Extrude032
FEATURE [Sketcher::SketchObject] Sketch095
  FullyConstrained = false
  MapMode = 5
  Placement = pos=(0,0,2) rot=(0,0,1;0rad)
  Support = -> [BaseFeature009]
  sketch-geometry (4):
    g0: LineSegment StartX=2 StartY=-107.3 StartZ=0 EndX=8 EndY=-107.3 EndZ=0
    g1: LineSegment StartX=8 StartY=-107.3 StartZ=0 EndX=8 EndY=-101.3 EndZ=0
    g2: LineSegment StartX=8 StartY=-101.3 StartZ=0 EndX=2 EndY=-101.3 EndZ=0
    g3: LineSegment StartX=2 StartY=-101.3 StartZ=0 EndX=2 EndY=-107.3 EndZ=0
  constraints (10):
    c: Coincident(g0,g1)
    c: Coincident(g1,g2)
    c: Coincident(g2,g3)
    c: Coincident(g3,g0)
    c: Horizontal(g0)
    c: Horizontal(g2)
    c: Vertical(g1)
    c: Vertical(g3)
    c: DistanceX(g2,g2) = 6
    c: DistanceY(g1,g1) = 6
FEATURE [Part::Extrusion] Extrude033  label="Extrude064"
  Base = -> Sketch095
  Dir = (0,0,1)
  DirMode = 2
  FaceMakerClass = Part::FaceMakerBullseye
  LengthFwd = 19.3
  LengthRev = 0
  Solid = true
  Symmetric = false
FEATURE [Sketcher::SketchObject] Sketch096
  FullyConstrained = false
  MapMode = 5
  Placement = pos=(0,0,21.3) rot=(0,0,1;0rad)
  Support = -> [Extrude033]
  sketch-geometry (1):
    g0: Circle CenterX=5 CenterY=-104.3 CenterZ=0 NormalX=0 NormalY=0 NormalZ=1 AngleXU=0 Radius=1.55
  constraints (1):
    c: Diameter(g0) = 3.1
FEATURE [PartDesign::Hole] Hole019  label="FRONT LEFT INSERT MNT"
  CustomThreadClearance = 0
  Depth = 2.5
  DepthType = 0
  Diameter = 3.2
  DrillForDepth = false
  DrillPoint = 1
  DrillPointAngle = 118
  HoleCutCountersinkAngle = 90
  HoleCutCustomValues = false
  HoleCutDepth = 0
  HoleCutDiameter = 6.1
  HoleCutType = 0
  ModelThread = false
  Profile = -> Sketch096
  Tapered = false
  TaperedAngle = 90
  ThreadClass = 0
  ThreadDepth = 2.5
  ThreadDepthType = 0
  ThreadDirection = 0
  ThreadFit = 0
  ThreadSize = 0
  ThreadType = 0
  Threaded = false
  UseCustomThreadClearance = false
FEATURE [Sketcher::SketchObject] Sketch097
  FullyConstrained = false
  MapMode = 5
  Placement = pos=(0,0,2) rot=(0,0,1;0rad)
  Support = -> [BaseFeature009]
  sketch-geometry (4):
    g0: LineSegment StartX=82.2 StartY=-107.3 StartZ=0 EndX=76.2 EndY=-107.3 EndZ=0
    g1: LineSegment StartX=76.2 StartY=-107.3 StartZ=0 EndX=76.2 EndY=-101.3 EndZ=0
    g2: LineSegment StartX=76.2 StartY=-101.3 StartZ=0 EndX=82.2 EndY=-101.3 EndZ=0
    g3: LineSegment StartX=82.2 StartY=-101.3 StartZ=0 EndX=82.2 EndY=-107.3 EndZ=0
  constraints (9):
    c: Coincident(g0,g1)
    c: Coincident(g1,g2)
    c: Coincident(g2,g3)
    c: Coincident(g3,g0)
    c: Horizontal(g0)
    c: Horizontal(g2)
    c: Vertical(g1)
    c: Vertical(g3)
    c: DistanceY(g1,g1) = 6
FEATURE [Part::Extrusion] Extrude034  label="Extrude065"
  Base = -> Sketch097
  Dir = (0,0,1)
  DirMode = 2
  FaceMakerClass = Part::FaceMakerBullseye
  LengthFwd = 19.3
  LengthRev = 0
  Solid = true
  Symmetric = false
FEATURE [Sketcher::SketchObject] Sketch098
  FullyConstrained = false
  MapMode = 5
  Placement = pos=(0,0,21.3) rot=(0,0,1;0rad)
  Support = -> [Extrude034]
  sketch-geometry (1):
    g0: Circle CenterX=79.2 CenterY=-104.3 CenterZ=0 NormalX=0 NormalY=0 NormalZ=1 AngleXU=0 Radius=1.6
  constraints (1):
    c: Diameter(g0) = 3.2
FEATURE [PartDesign::Hole] Hole020  label="FRONT RIGHT INSERT MNT"
  CustomThreadClearance = 0
  Depth = 2.3
  DepthType = 0
  Diameter = 3.2
  DrillForDepth = false
  DrillPoint = 1
  DrillPointAngle = 118
  HoleCutCountersinkAngle = 90
  HoleCutCustomValues = false
  HoleCutDepth = 0
  HoleCutDiameter = 6.1
  HoleCutType = 0
  ModelThread = false
  Profile = -> Sketch098
  Tapered = false
  TaperedAngle = 90
  ThreadClass = 0
  ThreadDepth = 2.3
  ThreadDepthType = 0
  ThreadDirection = 0
  ThreadFit = 0
  ThreadSize = 0
  ThreadType = 0
  Threaded = false
  UseCustomThreadClearance = false
FEATURE [Sketcher::SketchObject] Sketch099
  FullyConstrained = false
  MapMode = 5
  Placement = pos=(0,-16.37,0) rot=(1,0,0;1.5708rad)
  Support = -> [Pocket017]
  sketch-geometry (4):
    g0: LineSegment StartX=2 StartY=21.3 StartZ=0 EndX=7 EndY=21.3 EndZ=0
    g1: LineSegment StartX=7 StartY=21.3 StartZ=0 EndX=7 EndY=16.3 EndZ=0
    g2: LineSegment StartX=7 StartY=16.3 StartZ=0 EndX=2 EndY=16.3 EndZ=0
    g3: LineSegment StartX=2 StartY=16.3 StartZ=0 EndX=2 EndY=21.3 EndZ=0
  constraints (10):
    c: Coincident(g0,g1)
    c: Coincident(g1,g2)
    c: Coincident(g2,g3)
    c: Coincident(g3,g0)
    c: Horizontal(g0)
    c: Horizontal(g2)
    c: Vertical(g1)
    c: Vertical(g3)
    c: DistanceY(g1,g1) = 5
    c: DistanceX(g0,g0) = 5
FEATURE [Part::Extrusion] Extrude035  label="Extrude066"
  Base = -> Sketch099
  Dir = (0,-1,2e-16)
  DirMode = 2
  FaceMakerClass = Part::FaceMakerBullseye
  LengthFwd = 5
  LengthRev = 0
  Solid = true
  Symmetric = false
FEATURE [Sketcher::SketchObject] Sketch100
  FullyConstrained = false
  MapMode = 5
  Placement = pos=(0,4.7e-15,21.3) rot=(0,0,1;0rad)
  Support = -> [Extrude035]
  sketch-geometry (1):
    g0: Circle CenterX=4 CenterY=-18.4 CenterZ=0 NormalX=0 NormalY=0 NormalZ=1 AngleXU=0 Radius=1.6
  constraints (1):
    c: Diameter(g0) = 3.2
FEATURE [PartDesign::Hole] Hole021  label="BACK LEFT INSERT MNT"
  CustomThreadClearance = 0
  Depth = 2.2
  DepthType = 0
  Diameter = 3.2
  DrillForDepth = false
  DrillPoint = 1
  DrillPointAngle = 118
  HoleCutCountersinkAngle = 90
  HoleCutCustomValues = false
  HoleCutDepth = 0
  HoleCutDiameter = 6.1
  HoleCutType = 0
  ModelThread = false
  Profile = -> Sketch100
  Tapered = false
  TaperedAngle = 90
  ThreadClass = 0
  ThreadDepth = 2.2
  ThreadDepthType = 0
  ThreadDirection = 0
  ThreadFit = 0
  ThreadSize = 0
  ThreadType = 0
  Threaded = false
  UseCustomThreadClearance = false
FEATURE [Sketcher::SketchObject] Sketch101
  FullyConstrained = false
  MapMode = 5
  Placement = pos=(0,-16.37,0) rot=(1,0,0;1.5708rad)
  Support = -> [Pocket017]
  sketch-geometry (4):
    g0: LineSegment StartX=82.2 StartY=21.3 StartZ=0 EndX=77.2 EndY=21.3 EndZ=0
    g1: LineSegment StartX=77.2 StartY=21.3 StartZ=0 EndX=77.2 EndY=16.3 EndZ=0
    g2: LineSegment StartX=77.2 StartY=16.3 StartZ=0 EndX=82.2 EndY=16.3 EndZ=0
    g3: LineSegment StartX=82.2 StartY=16.3 StartZ=0 EndX=82.2 EndY=21.3 EndZ=0
  constraints (10):
    c: Coincident(g0,g1)
    c: Coincident(g1,g2)
    c: Coincident(g2,g3)
    c: Coincident(g3,g0)
    c: Horizontal(g0)
    c: Horizontal(g2)
    c: Vertical(g1)
    c: Vertical(g3)
    c: DistanceX(g0,g0) = 5
    c: DistanceY(g3,g3) = 5
FEATURE [Part::Extrusion] Extrude036  label="Extrude067"
  Base = -> Sketch101
  Dir = (0,-1,2e-16)
  DirMode = 2
  FaceMakerClass = Part::FaceMakerBullseye
  LengthFwd = 5
  LengthRev = 0
  Solid = true
  Symmetric = false
FEATURE [Sketcher::SketchObject] Sketch102
  FullyConstrained = false
  MapMode = 5
  Placement = pos=(0,4.7e-15,21.3) rot=(0,0,1;0rad)
  Support = -> [Extrude036]
  sketch-geometry (1):
    g0: Circle CenterX=80 CenterY=-18.4 CenterZ=0 NormalX=0 NormalY=0 NormalZ=1 AngleXU=0 Radius=1.6
  constraints (1):
    c: Diameter(g0) = 3.2
FEATURE [PartDesign::Hole] Hole022  label="BACK RIGHT INSERT MNT"
  CustomThreadClearance = 0
  Depth = 2.3
  DepthType = 0
  Diameter = 3.2
  DrillForDepth = false
  DrillPoint = 1
  DrillPointAngle = 118
  HoleCutCountersinkAngle = 90
  HoleCutCustomValues = false
  HoleCutDepth = 0
  HoleCutDiameter = 6.1
  HoleCutType = 0
  ModelThread = false
  Profile = -> Sketch102
  Tapered = false
  TaperedAngle = 90
  ThreadClass = 0
  ThreadDepth = 2.3
  ThreadDepthType = 0
  ThreadDirection = 0
  ThreadFit = 0
  ThreadSize = 0
  ThreadType = 0
  Threaded = false
  UseCustomThreadClearance = false
FEATURE [Sketcher::SketchObject] Sketch103
  FullyConstrained = false
  MapMode = 5
  Support = -> [XY_Plane109]
  sketch-geometry (4):
    g0: LineSegment StartX=0 StartY=-14.3705 StartZ=0 EndX=84.2 EndY=-14.3705 EndZ=0
    g1: LineSegment StartX=84.2 StartY=-14.3705 StartZ=0 EndX=84.2 EndY=-109.301 EndZ=0
    g2: LineSegment StartX=84.2 StartY=-109.301 StartZ=0 EndX=0 EndY=-109.301 EndZ=0
    g3: LineSegment StartX=0 StartY=-109.301 StartZ=0 EndX=0 EndY=-14.3705 EndZ=0
  constraints (11):
    c: Coincident(g0,g1)
    c: Coincident(g1,g2)
    c: Coincident(g2,g3)
    c: Coincident(g3,g0)
    c: Horizontal(g0)
    c: Horizontal(g2)
    c: Vertical(g1)
    c: Vertical(g3)
    c: PointOnObject(g0,g-2)
    c: DistanceX(g2,g2) = 84.2
    c: DistanceY(g1,g1) = 94.93
FEATURE [Part::Extrusion] Extrude037  label="Extrude068"
  Base = -> Sketch103
  Dir = (0,0,1)
  DirMode = 2
  FaceMakerClass = Part::FaceMakerBullseye
  LengthFwd = 1.5
  LengthRev = 0
  Solid = true
  Symmetric = false
FEATURE [Sketcher::SketchObject] Sketch104
  FullyConstrained = false
  MapMode = 5
  Placement = pos=(0,0,1.5) rot=(0,0,1;0rad)
  Support = -> [Extrude037]
  sketch-geometry (4):
    g0: Circle CenterX=4 CenterY=-18.3995 CenterZ=0 NormalX=0 NormalY=0 NormalZ=1 AngleXU=0 Radius=1.6
    g1: Circle CenterX=80 CenterY=-18.4 CenterZ=0 NormalX=0 NormalY=0 NormalZ=1 AngleXU=0 Radius=1.6
    g2: Circle CenterX=79.2 CenterY=-104.3 CenterZ=0 NormalX=0 NormalY=0 NormalZ=1 AngleXU=0 Radius=1.6
    g3: Circle CenterX=5 CenterY=-104.3 CenterZ=0 NormalX=0 NormalY=0 NormalZ=1 AngleXU=0 Radius=1.6
  constraints (4):
    c: Diameter(g0) = 3.2
    c: Diameter(g1) = 3.2
    c: Diameter(g2) = 3.2
    c: Diameter(g3) = 3.2
FEATURE [PartDesign::Hole] Hole023  label="TOP PLATE WITH COUNTERSUNK HOLES"
  CustomThreadClearance = 0
  Depth = 2
  DepthType = 0
  Diameter = 2
  DrillForDepth = false
  DrillPoint = 0
  DrillPointAngle = 118
  HoleCutCountersinkAngle = 90
  HoleCutCustomValues = false
  HoleCutDepth = 2
  HoleCutDiameter = 3.8
  HoleCutType = 2
  ModelThread = false
  Profile = -> Sketch104
  Tapered = false
  TaperedAngle = 90
  ThreadClass = 0
  ThreadDepth = 2
  ThreadDepthType = 0
  ThreadDirection = 0
  ThreadFit = 0
  ThreadSize = 0
  ThreadType = 0
  Threaded = false
  UseCustomThreadClearance = false
FEATURE [Sketcher::SketchObject] Sketch105
  FullyConstrained = false
  MapMode = 5
  Placement = pos=(0,0,2) rot=(0,0,1;0rad)
  Support = -> [BaseFeature009]
  sketch-geometry (7):
    g0: LineSegment StartX=2 StartY=-99.8 StartZ=0 EndX=82.2 EndY=-99.8 EndZ=0
    g1: LineSegment StartX=2 StartY=-99.9 StartZ=0 EndX=42.1 EndY=-99.9 EndZ=0
    g2: LineSegment StartX=42.1 StartY=-100 StartZ=0 EndX=37.85 EndY=-100 EndZ=0
    g3: LineSegment StartX=37.85 StartY=-99.7927 StartZ=0 EndX=46.4 EndY=-99.7927 EndZ=0
    g4: LineSegment StartX=46.4 StartY=-99.7927 StartZ=0 EndX=46.4 EndY=-107.303 EndZ=0
    g5: LineSegment StartX=46.4 StartY=-107.303 StartZ=0 EndX=37.85 EndY=-107.303 EndZ=0
    g6: LineSegment StartX=37.85 StartY=-107.303 StartZ=0 EndX=37.85 EndY=-99.7927 EndZ=0
  constraints (15):
    c: Horizontal(g0)
    c: DistanceX(g0,g0) = 80.2
    c: Horizontal(g1)
    c: DistanceX(g1,g1) = 40.1
    c: Horizontal(g2)
    c: Coincident(g3,g4)
    c: Coincident(g4,g5)
    c: Coincident(g5,g6)
    c: Coincident(g6,g3)
    c: Horizontal(g3)
    c: Horizontal(g5)
    c: Vertical(g4)
    c: Vertical(g6)
    c: DistanceY(g4,g4) = 7.51
    c: DistanceX(g3,g3) = 8.55
FEATURE [Part::Extrusion] Extrude038  label="Extrude069"
  Base = -> Sketch105
  Dir = (0,0,1)
  DirMode = 2
  FaceMakerClass = Part::FaceMakerBullseye
  LengthFwd = 5.5
  LengthRev = 0
  Solid = true
  Symmetric = false
FEATURE [Sketcher::SketchObject] Sketch106
  FullyConstrained = false
  MapMode = 5
  Placement = pos=(0,0,7.5) rot=(0,0,1;0rad)
  Support = -> [Extrude038]
  sketch-geometry (1):
    g0: Circle CenterX=42.15 CenterY=-103.5 CenterZ=0 NormalX=0 NormalY=0 NormalZ=1 AngleXU=0 Radius=2.25
  constraints (1):
    c: Diameter(g0) = 4.5
FEATURE [PartDesign::Hole] Hole024  label="FRONT LOCK SLOT"
  CustomThreadClearance = 0
  Depth = 5.5
  DepthType = 0
  Diameter = 4.5
  DrillForDepth = false
  DrillPoint = 0
  DrillPointAngle = 118
  HoleCutCountersinkAngle = 90
  HoleCutCustomValues = false
  HoleCutDepth = 0
  HoleCutDiameter = 6.1
  HoleCutType = 0
  ModelThread = false
  Profile = -> Sketch106
  Tapered = false
  TaperedAngle = 90
  ThreadClass = 0
  ThreadDepth = 5.5
  ThreadDepthType = 0
  ThreadDirection = 0
  ThreadFit = 0
  ThreadSize = 0
  ThreadType = 0
  Threaded = false
  UseCustomThreadClearance = false
FEATURE [Sketcher::SketchObject] Sketch107
  FullyConstrained = false
  MapMode = 5
  Placement = pos=(0,0,0) rot=(1,0,0;3.14159rad)
  Support = -> [Hole018]
  sketch-geometry (1):
    g0: Circle CenterX=-134 CenterY=113.5 CenterZ=0 NormalX=0 NormalY=0 NormalZ=1 AngleXU=0 Radius=2.125
  constraints (1):
    c: Diameter(g0) = 4.25
FEATURE [Part::Extrusion] Extrude039  label="SPRING CYLINDER"
  Base = -> Sketch107
  Dir = (0,0,-1)
  DirMode = 2
  FaceMakerClass = Part::FaceMakerBullseye
  LengthFwd = 9
  LengthRev = 0
  Solid = true
  Symmetric = false
FEATURE [Sketcher::SketchObject] Sketch108
  FullyConstrained = false
  MapMode = 5
  Placement = pos=(0,0,1.5) rot=(0,0,1;0rad)
  Support = -> [Hole023]
  sketch-geometry (4):
    g0: LineSegment StartX=36.86 StartY=-100.71 StartZ=0 EndX=47.46 EndY=-100.71 EndZ=0
    g1: LineSegment StartX=47.46 StartY=-100.71 StartZ=0 EndX=47.46 EndY=-106.31 EndZ=0
    g2: LineSegment StartX=47.46 StartY=-106.31 StartZ=0 EndX=36.86 EndY=-106.31 EndZ=0
    g3: LineSegment StartX=36.86 StartY=-106.31 StartZ=0 EndX=36.86 EndY=-100.71 EndZ=0
  constraints (10):
    c: Coincident(g0,g1)
    c: Coincident(g1,g2)
    c: Coincident(g2,g3)
    c: Coincident(g3,g0)
    c: Horizontal(g0)
    c: Horizontal(g2)
    c: Vertical(g1)
    c: Vertical(g3)
    c: DistanceX(g0,g0) = 10.6
    c: DistanceY(g3,g3) = 5.6
FEATURE [PartDesign::Pocket] Pocket020  label="TOP PLATE WITH LOCK POCKET"
  BaseFeature = -> Hole023
  Direction = (0,0,-1)
  Length = 1.5
  Length2 = 5
  Profile = -> Sketch108
  ReferenceAxis = -> Sketch108 [N_Axis]
  Type = 0
FEATURE [PartDesign::Body] Body013  label="TOP PLATE BODY"
  Group = -> [Sketch104,Hole023,Sketch108,Pocket020]
  Origin = -> Origin109
  Tip = -> Pocket020
FEATURE [App::Part] Part026  label="top plate"
  Group = -> [Body013,Sketch103,Extrude037]
  Origin = -> Origin108
  Placement = pos=(0,0,21.28) rot=(0,0,1;0rad)
FEATURE [Sketcher::SketchObject] Sketch109
  FullyConstrained = false
  MapMode = 5
  Placement = pos=(0,0,7) rot=(0,0,1;0rad)
  Support = -> [Hole018]
  sketch-geometry (4):
    g0: LineSegment StartX=-139 StartY=-111 StartZ=0 EndX=-129 EndY=-111 EndZ=0
    g1: LineSegment StartX=-129 StartY=-111 StartZ=0 EndX=-129 EndY=-116 EndZ=0
    g2: LineSegment StartX=-129 StartY=-116 StartZ=0 EndX=-139 EndY=-116 EndZ=0
    g3: LineSegment StartX=-139 StartY=-116 StartZ=0 EndX=-139 EndY=-111 EndZ=0
  constraints (10):
    c: Coincident(g0,g1)
    c: Coincident(g1,g2)
    c: Coincident(g2,g3)
    c: Coincident(g3,g0)
    c: Horizontal(g0)
    c: Horizontal(g2)
    c: Vertical(g1)
    c: Vertical(g3)
    c: DistanceY(g1,g1) = 5
    c: DistanceX(g0,g0) = 10
FEATURE [Part::Extrusion] Extrude040  label="Extrude070"
  Base = -> Sketch109
  Dir = (0,0,1)
  DirMode = 2
  FaceMakerClass = Part::FaceMakerBullseye
  LengthFwd = 4.5
  LengthRev = 0
  Solid = true
  Symmetric = false
FEATURE [PartDesign::FeatureBase] BaseFeature010
  BaseFeature = -> Extrude040
FEATURE [Sketcher::SketchObject] Sketch110
  FullyConstrained = false
  MapMode = 5
  Placement = pos=(-129,0,0) rot=(0.57735,0.57735,0.57735;2.0944rad)
  Support = -> [Extrude040]
  sketch-geometry (3):
    g0: LineSegment StartX=-110.99 StartY=8.49 StartZ=0 EndX=-116 EndY=11.5 EndZ=0
    g1: LineSegment StartX=-116 StartY=11.5 StartZ=0 EndX=-110.99 EndY=11.5 EndZ=0
    g2: LineSegment StartX=-110.99 StartY=11.5 StartZ=0 EndX=-110.99 EndY=8.49 EndZ=0
  constraints (7):
    c: Coincident(g0,g1)
    c: Horizontal(g1)
    c: Coincident(g1,g2)
    c: Coincident(g2,g0)
    c: Vertical(g2)
    c: DistanceY(g2,g2) = 3.01
    c: DistanceX(g1,g1) = 5.01
FEATURE [PartDesign::Pocket] Pocket019  label="LOCK SLIDE HOOK"
  Direction = (-1,0,0)
  Length = 10
  Length2 = 5
  Profile = -> Sketch110
  ReferenceAxis = -> Sketch110 [N_Axis]
  Type = 0
FEATURE [Sketcher::SketchObject] Sketch111
  FullyConstrained = false
  MapMode = 5
  Support = -> [XY_Plane102]
  sketch-geometry (6):
    g0: LineSegment StartX=-145 StartY=-119.61 StartZ=0 EndX=-145 EndY=-110 EndZ=0
    g1: LineSegment StartX=-123 StartY=-119.61 StartZ=0 EndX=-123 EndY=-110 EndZ=0
    g2: LineSegment StartX=-147 StartY=-110 StartZ=0 EndX=-121 EndY=-110 EndZ=0
    g3: LineSegment StartX=-121 StartY=-110 StartZ=0 EndX=-121 EndY=-117 EndZ=0
    g4: LineSegment StartX=-121 StartY=-117 StartZ=0 EndX=-147 EndY=-117 EndZ=0
    g5: LineSegment StartX=-147 StartY=-117 StartZ=0 EndX=-147 EndY=-110 EndZ=0
  constraints (12):
    c: Vertical(g0)
    c: Vertical(g1)
    c: Coincident(g2,g3)
    c: Coincident(g3,g4)
    c: Coincident(g4,g5)
    c: Coincident(g5,g2)
    c: Horizontal(g2)
    c: Horizontal(g4)
    c: Vertical(g3)
    c: Vertical(g5)
    c: DistanceY(g5,g5) = 7
    c: DistanceX(g2,g2) = 26
FEATURE [Part::Extrusion] Extrude047  label="Extrude076"
  Base = -> Sketch111
  Dir = (0,0,1)
  DirMode = 2
  FaceMakerClass = Part::FaceMakerBullseye
  LengthFwd = 7
  LengthRev = 0
  Solid = true
  Symmetric = false
FEATURE [PartDesign::FeatureBase] BaseFeature016
  BaseFeature = -> Extrude047
FEATURE [Sketcher::SketchObject] Sketch112
  FullyConstrained = false
  MapMode = 5
  Placement = pos=(0,-109.3,0) rot=(1,0,0;1.5708rad)
  Support = -> [Extrude032]
  sketch-geometry (4):
    g0: LineSegment StartX=40.86 StartY=19.75 StartZ=0 EndX=43.5 EndY=19.75 EndZ=0
    g1: LineSegment StartX=43.5 StartY=19.75 StartZ=0 EndX=43.5 EndY=12.6 EndZ=0
    g2: LineSegment StartX=43.5 StartY=12.6 StartZ=0 EndX=40.86 EndY=12.6 EndZ=0
    g3: LineSegment StartX=40.86 StartY=12.6 StartZ=0 EndX=40.86 EndY=19.75 EndZ=0
  constraints (10):
    c: Coincident(g0,g1)
    c: Coincident(g1,g2)
    c: Coincident(g2,g3)
    c: Coincident(g3,g0)
    c: Horizontal(g0)
    c: Horizontal(g2)
    c: Vertical(g1)
    c: Vertical(g3)
    c: DistanceX(g0,g0) = 2.64
    c: DistanceY(g3,g3) = 7.15
FEATURE [PartDesign::Pocket] Pocket021  label="FRONT WALL WITH HANDLE SLOT"
  BaseFeature = -> BaseFeature011
  Direction = (0,1,-2e-16)
  Length = 2
  Length2 = 5
  Profile = -> Sketch112
  ReferenceAxis = -> Sketch112 [N_Axis]
  Type = 0
FEATURE [Sketcher::SketchObject] Sketch113
  FullyConstrained = false
  MapMode = 5
  Placement = pos=(2,-4e-16,4e-16) rot=(0.57735,0.57735,0.57735;2.0944rad)
  Support = -> [Extrude041]
  sketch-geometry (1):
    g0: Circle CenterX=-125.95 CenterY=3.5 CenterZ=0 NormalX=0 NormalY=0 NormalZ=1 AngleXU=0 Radius=0.75
  constraints (1):
    c: Diameter(g0) = 1.5
FEATURE [PartDesign::Hole] Hole025  label="BASE HANDLE INSERT"
  CustomThreadClearance = 0
  Depth = 2
  DepthType = 0
  Diameter = 1.5
  DrillForDepth = false
  DrillPoint = 1
  DrillPointAngle = 118
  HoleCutCountersinkAngle = 90
  HoleCutCustomValues = false
  HoleCutDepth = 0
  HoleCutDiameter = 6.1
  HoleCutType = 0
  ModelThread = false
  Profile = -> Sketch113
  Tapered = false
  TaperedAngle = 90
  ThreadClass = 0
  ThreadDepth = 2
  ThreadDepthType = 0
  ThreadDirection = 0
  ThreadFit = 0
  ThreadSize = 0
  ThreadType = 0
  Threaded = false
  UseCustomThreadClearance = false
FEATURE [Sketcher::SketchObject] Sketch114
  FullyConstrained = false
  MapMode = 5
  Placement = pos=(0,-28.49,0) rot=(1,0,0;1.5708rad)
  Support = -> [Extrude027]
  sketch-geometry (8):
    g0: ArcOfCircle CenterX=11.5 CenterY=21.374 CenterZ=0 NormalX=0 NormalY=0 NormalZ=1 AngleXU=0 Radius=7.50005 StartAngle=3.13813 EndAngle=6.28665
    g1: LineSegment StartX=4 StartY=21.4 StartZ=0 EndX=19 EndY=21.4 EndZ=0
    g2: ArcOfCircle CenterX=32 CenterY=21.3845 CenterZ=0 NormalX=0 NormalY=0 NormalZ=1 AngleXU=0 Radius=8.00001 StartAngle=3.13966 EndAngle=6.28512
    g3: LineSegment StartX=24 StartY=21.4 StartZ=0 EndX=40 EndY=21.4 EndZ=0
    g4: ArcOfCircle CenterX=52.2 CenterY=21.3636 CenterZ=0 NormalX=0 NormalY=0 NormalZ=1 AngleXU=0 Radius=7.80009 StartAngle=3.13692 EndAngle=6.28785
    g5: LineSegment StartX=60 StartY=21.4 StartZ=0 EndX=44.4 EndY=21.4 EndZ=0
    g6: ArcOfCircle CenterX=72.5 CenterY=21.2875 CenterZ=0 NormalX=0 NormalY=0 NormalZ=1 AngleXU=0 Radius=7.50084 StartAngle=3.12659 EndAngle=6.29819
    g7: LineSegment StartX=80 StartY=21.4 StartZ=0 EndX=65 EndY=21.4 EndZ=0
  constraints (19):
    c: Coincident(g1,g0)
    c: Coincident(g1,g0)
    c: Horizontal(g1)
    c: DistanceX(g1,g1) = 15
    c: Diameter(g0) = 15.0001
    c: Coincident(g3,g2)
    c: Coincident(g3,g2)
    c: Horizontal(g3)
    c: DistanceX(g3,g3) = 16
    c: Diameter(g2) = 16
    c: Coincident(g5,g4)
    c: Coincident(g5,g4)
    c: Horizontal(g5)
    c: DistanceX(g5,g5) = 15.6
    c: Diameter(g4) = 15.6002
    c: Coincident(g7,g6)
    c: Coincident(g7,g6)
    c: Horizontal(g7)
    c: DistanceX(g7,g7) = 15
FEATURE [PartDesign::Pocket] Pocket022  label="cell walls"
  BaseFeature = -> BaseFeature012
  Direction = (0,1,-2e-16)
  Length = 5
  Length2 = 5
  Profile = -> Sketch114
  ReferenceAxis = -> Sketch114 [N_Axis]
  Type = 0
FEATURE [PartDesign::FeatureBase] BaseFeature013
  BaseFeature = -> Pocket022
FEATURE [Sketcher::SketchObject] Sketch115
  FullyConstrained = false
  MapMode = 5
  Placement = pos=(2,-4e-16,4e-16) rot=(0.57735,0.57735,0.57735;2.0944rad)
  Support = -> [Hole025]
  sketch-geometry (9):
    g0: LineSegment StartX=-133.3 StartY=5 StartZ=0 EndX=-133.3 EndY=3 EndZ=0
    g1: LineSegment StartX=-133.3 StartY=3 StartZ=0 EndX=-131.8 EndY=3 EndZ=0
    g2: LineSegment StartX=-131.8 StartY=3 StartZ=0 EndX=-131.8 EndY=-7 EndZ=0
    g3: LineSegment StartX=-131.8 StartY=-7 StartZ=0 EndX=-133.3 EndY=-7 EndZ=0
    g4: LineSegment StartX=-133.3 StartY=-7 StartZ=0 EndX=-133.3 EndY=-9 EndZ=0
    g5: LineSegment StartX=-133.3 StartY=-9 StartZ=0 EndX=-130.3 EndY=-9 EndZ=0
    g6: LineSegment StartX=-130.3 StartY=-9 StartZ=0 EndX=-130.3 EndY=2 EndZ=0
    g7: LineSegment StartX=-130.3 StartY=2 StartZ=0 EndX=-130.3 EndY=5 EndZ=0
    g8: LineSegment StartX=-130.3 StartY=5 StartZ=0 EndX=-133.3 EndY=5 EndZ=0
  constraints (25):
    c: Vertical(g0)
    c: Coincident(g0,g1)
    c: Horizontal(g1)
    c: Coincident(g1,g2)
    c: Vertical(g2)
    c: Coincident(g2,g3)
    c: Horizontal(g3)
    c: Coincident(g3,g4)
    c: Vertical(g4)
    c: Coincident(g4,g5)
    c: Horizontal(g5)
    c: Coincident(g5,g6)
    c: Vertical(g6)
    c: Coincident(g6,g7)
    c: Vertical(g7)
    c: Coincident(g7,g8)
    c: Coincident(g8,g0)
    c: Horizontal(g8)
    c: DistanceX(g8,g8) = 3
    c: DistanceX(g1,g1) = 1.5
    c: DistanceX(g3,g3) = 1.50001
    c: DistanceY(g6,g6) = 11
    c: DistanceY(g2,g2) = 10
    c: DistanceY(g4,g4) = 2
    c: DistanceY(g0,g0) = 2
FEATURE [Part::Extrusion] Extrude042  label="Extrude072"
  Base = -> Sketch115
  Dir = (1,-2e-16,2e-16)
  DirMode = 2
  FaceMakerClass = Part::FaceMakerBullseye
  LengthFwd = 10
  LengthRev = 0
  Solid = true
  Symmetric = false
FEATURE [Sketcher::SketchObject] Sketch116
  FullyConstrained = false
  MapMode = 5
  Placement = pos=(-3e-16,0,0) rot=(-0.57735,0.57735,0.57735;4.18879rad)
  Support = -> [Hole025]
  sketch-geometry (9):
    g0: LineSegment StartX=133.3 StartY=5 StartZ=0 EndX=133.3 EndY=3 EndZ=0
    g1: LineSegment StartX=133.3 StartY=3 StartZ=0 EndX=131.8 EndY=3 EndZ=0
    g2: LineSegment StartX=131.8 StartY=3 StartZ=0 EndX=131.8 EndY=-7 EndZ=0
    g3: LineSegment StartX=131.8 StartY=-7 StartZ=0 EndX=133.3 EndY=-7 EndZ=0
    g4: LineSegment StartX=133.3 StartY=-7 StartZ=0 EndX=133.3 EndY=-9 EndZ=0
    g5: LineSegment StartX=133.3 StartY=-9 StartZ=0 EndX=130.3 EndY=-9 EndZ=0
    g6: LineSegment StartX=130.3 StartY=-9 StartZ=0 EndX=130.3 EndY=2 EndZ=0
    g7: LineSegment StartX=130.3 StartY=2 StartZ=0 EndX=130.3 EndY=5 EndZ=0
    g8: LineSegment StartX=130.3 StartY=5 StartZ=0 EndX=133.3 EndY=5 EndZ=0
  constraints (25):
    c: Vertical(g0)
    c: Coincident(g0,g1)
    c: Horizontal(g1)
    c: Coincident(g1,g2)
    c: Vertical(g2)
    c: Coincident(g2,g3)
    c: Horizontal(g3)
    c: Coincident(g3,g4)
    c: Vertical(g4)
    c: Coincident(g4,g5)
    c: Horizontal(g5)
    c: Coincident(g5,g6)
    c: Vertical(g6)
    c: Coincident(g6,g7)
    c: Vertical(g7)
    c: Coincident(g7,g8)
    c: Coincident(g8,g0)
    c: Horizontal(g8)
    c: DistanceX(g8,g8) = 3
    c: DistanceX(g1,g1) = 1.49999
    c: DistanceX(g5,g5) = 3
    c: DistanceY(g6,g6) = 11
    c: DistanceY(g4,g4) = 2
    c: DistanceY(g2,g2) = 10
    c: DistanceY(g0,g0) = 2
FEATURE [Part::Extrusion] Extrude043  label="Extrude073"
  Base = -> Sketch116
  Dir = (-1,2e-16,-2e-16)
  DirMode = 2
  FaceMakerClass = Part::FaceMakerBullseye
  LengthFwd = 10
  LengthRev = 0
  Solid = true
  Symmetric = false
FEATURE [Sketcher::SketchObject] Sketch117
  FullyConstrained = false
  MapMode = 5
  Placement = pos=(0,-109.3,0) rot=(1,0,0;1.5708rad)
  Support = -> [Pocket021]
  sketch-geometry (32):
    g0: Circle CenterX=10 CenterY=16 CenterZ=0 NormalX=0 NormalY=0 NormalZ=1 AngleXU=0 Radius=0.5
    g1: Circle CenterX=11.3 CenterY=16 CenterZ=0 NormalX=0 NormalY=0 NormalZ=1 AngleXU=0 Radius=0.5
    g2: Circle CenterX=10 CenterY=14.7 CenterZ=0 NormalX=0 NormalY=0 NormalZ=1 AngleXU=0 Radius=0.5
    g3: Circle CenterX=11.3 CenterY=14.7 CenterZ=0 NormalX=0 NormalY=0 NormalZ=1 AngleXU=0 Radius=0.5
    g4: Circle CenterX=12.6 CenterY=14.7 CenterZ=0 NormalX=0 NormalY=0 NormalZ=1 AngleXU=0 Radius=0.5
    g5: Circle CenterX=13.9 CenterY=14.7 CenterZ=0 NormalX=0 NormalY=0 NormalZ=1 AngleXU=0 Radius=0.5
    g6: Circle CenterX=15.2 CenterY=14.7 CenterZ=0 NormalX=0 NormalY=0 NormalZ=1 AngleXU=0 Radius=0.5
    g7: Circle CenterX=12.6 CenterY=16 CenterZ=0 NormalX=0 NormalY=0 NormalZ=1 AngleXU=0 Radius=0.5
    g8: Circle CenterX=13.9 CenterY=16 CenterZ=0 NormalX=0 NormalY=0 NormalZ=1 AngleXU=0 Radius=0.5
    g9: Circle CenterX=15.2 CenterY=16 CenterZ=0 NormalX=0 NormalY=0 NormalZ=1 AngleXU=0 Radius=0.5
    g10: Circle CenterX=10 CenterY=13.4 CenterZ=0 NormalX=0 NormalY=0 NormalZ=1 AngleXU=0 Radius=0.5
    g11: Circle CenterX=11.3 CenterY=13.4 CenterZ=0 NormalX=0 NormalY=0 NormalZ=1 AngleXU=0 Radius=0.5
    g12: Circle CenterX=12.6 CenterY=13.4 CenterZ=0 NormalX=0 NormalY=0 NormalZ=1 AngleXU=0 Radius=0.5
    g13: Circle CenterX=13.9 CenterY=13.4 CenterZ=0 NormalX=0 NormalY=0 NormalZ=1 AngleXU=0 Radius=0.5
    g14: Circle CenterX=15.2 CenterY=13.4 CenterZ=0 NormalX=0 NormalY=0 NormalZ=1 AngleXU=0 Radius=0.5
    g15: Circle CenterX=10 CenterY=12.1 CenterZ=0 NormalX=0 NormalY=0 NormalZ=1 AngleXU=0 Radius=0.5
    g16: Circle CenterX=11.3 CenterY=12.1 CenterZ=0 NormalX=0 NormalY=0 NormalZ=1 AngleXU=0 Radius=0.5
    g17: Circle CenterX=12.6 CenterY=12.1 CenterZ=0 NormalX=0 NormalY=0 NormalZ=1 AngleXU=0 Radius=0.5
    g18: Circle CenterX=13.9 CenterY=12.1 CenterZ=0 NormalX=0 NormalY=0 NormalZ=1 AngleXU=0 Radius=0.5
    g19: Circle CenterX=15.2 CenterY=12.1 CenterZ=0 NormalX=0 NormalY=0 NormalZ=1 AngleXU=0 Radius=0.5
    g20: Circle CenterX=16.5 CenterY=16 CenterZ=0 NormalX=0 NormalY=0 NormalZ=1 AngleXU=0 Radius=0.5
    g21: Circle CenterX=16.5 CenterY=14.7 CenterZ=0 NormalX=0 NormalY=0 NormalZ=1 AngleXU=0 Radius=0.5
    g22: Circle CenterX=16.5 CenterY=13.4 CenterZ=0 NormalX=0 NormalY=0 NormalZ=1 AngleXU=0 Radius=0.5
    g23: Circle CenterX=16.5 CenterY=12.1 CenterZ=0 NormalX=0 NormalY=0 NormalZ=1 AngleXU=0 Radius=0.5
    g24: Circle CenterX=17.8 CenterY=16 CenterZ=0 NormalX=0 NormalY=0 NormalZ=1 AngleXU=0 Radius=0.5
    g25: Circle CenterX=19.1 CenterY=16 CenterZ=0 NormalX=0 NormalY=0 NormalZ=1 AngleXU=0 Radius=0.5
    g26: Circle CenterX=17.8 CenterY=14.7 CenterZ=0 NormalX=0 NormalY=0 NormalZ=1 AngleXU=0 Radius=0.5
    g27: Circle CenterX=19.1 CenterY=14.7 CenterZ=0 NormalX=0 NormalY=0 NormalZ=1 AngleXU=0 Radius=0.5
    g28: Circle CenterX=17.8 CenterY=13.4 CenterZ=0 NormalX=0 NormalY=0 NormalZ=1 AngleXU=0 Radius=0.5
    g29: Circle CenterX=19.1 CenterY=13.4 CenterZ=0 NormalX=0 NormalY=0 NormalZ=1 AngleXU=0 Radius=0.5
    g30: Circle CenterX=17.8 CenterY=12.1 CenterZ=0 NormalX=0 NormalY=0 NormalZ=1 AngleXU=0 Radius=0.5
    g31: Circle CenterX=19.1 CenterY=12.1 CenterZ=0 NormalX=0 NormalY=0 NormalZ=1 AngleXU=0 Radius=0.5
  constraints (32):
    c: Diameter(g0) = 1
    c: Diameter(g1) = 1
    c: Diameter(g7) = 1
    c: Diameter(g8) = 1
    c: Diameter(g9) = 1
    c: Diameter(g2) = 1
    c: Diameter(g3) = 1
    c: Diameter(g4) = 1
    c: Diameter(g5) = 1
    c: Diameter(g6) = 1
    c: Diameter(g10) = 1
    c: Diameter(g11) = 1
    c: Diameter(g12) = 1
    c: Diameter(g13) = 1
    c: Diameter(g14) = 1
    c: Diameter(g19) = 1
    c: Diameter(g18) = 1
    c: Diameter(g17) = 1
    c: Diameter(g16) = 1
    c: Diameter(g15) = 1
    c: Diameter(g20) = 1
    c: Diameter(g21) = 1
    c: Diameter(g22) = 1
    c: Diameter(g23) = 1
    c: Diameter(g24) = 1
    c: Diameter(g26) = 1
    c: Diameter(g28) = 1
    c: Diameter(g30) = 1
    c: Diameter(g31) = 1
    c: Diameter(g29) = 1
    c: Diameter(g27) = 1
    c: Diameter(g25) = 1
FEATURE [PartDesign::Hole] Hole026
  CustomThreadClearance = 0
  Depth = 2
  DepthType = 0
  Diameter = 1
  DrillForDepth = false
  DrillPoint = 0
  DrillPointAngle = 118
  HoleCutCountersinkAngle = 90
  HoleCutCustomValues = false
  HoleCutDepth = 0
  HoleCutDiameter = 6.1
  HoleCutType = 0
  ModelThread = false
  Profile = -> Sketch117
  Tapered = false
  TaperedAngle = 90
  ThreadClass = 0
  ThreadDepth = 2
  ThreadDepthType = 0
  ThreadDirection = 0
  ThreadFit = 0
  ThreadSize = 0
  ThreadType = 0
  Threaded = false
  UseCustomThreadClearance = false
FEATURE [Sketcher::SketchObject] Sketch118
  FullyConstrained = false
  MapMode = 5
  Placement = pos=(0,-99.794,0) rot=(1,0,0;1.5708rad)
  Support = -> [Pocket022]
  sketch-geometry (8):
    g0: ArcOfCircle CenterX=11.5 CenterY=21.374 CenterZ=0 NormalX=0 NormalY=0 NormalZ=1 AngleXU=0 Radius=7.50005 StartAngle=3.13813 EndAngle=6.28665
    g1: LineSegment StartX=4 StartY=21.4 StartZ=0 EndX=19 EndY=21.4 EndZ=0
    g2: ArcOfCircle CenterX=32 CenterY=21.3845 CenterZ=0 NormalX=0 NormalY=0 NormalZ=1 AngleXU=0 Radius=8.00001 StartAngle=3.13966 EndAngle=6.28512
    g3: LineSegment StartX=24 StartY=21.4 StartZ=0 EndX=40 EndY=21.4 EndZ=0
    g4: ArcOfCircle CenterX=52.2 CenterY=21.3636 CenterZ=0 NormalX=0 NormalY=0 NormalZ=1 AngleXU=0 Radius=7.80009 StartAngle=3.13692 EndAngle=6.28785
    g5: LineSegment StartX=60 StartY=21.4 StartZ=0 EndX=44.4 EndY=21.4 EndZ=0
    g6: ArcOfCircle CenterX=72.5 CenterY=21.2875 CenterZ=0 NormalX=0 NormalY=0 NormalZ=1 AngleXU=0 Radius=7.50084 StartAngle=3.12659 EndAngle=6.29819
    g7: LineSegment StartX=80 StartY=21.4 StartZ=0 EndX=65 EndY=21.4 EndZ=0
  constraints (19):
    c: Coincident(g1,g0)
    c: Coincident(g1,g0)
    c: Horizontal(g1)
    c: DistanceX(g1,g1) = 15
    c: Diameter(g0) = 15.0001
    c: Coincident(g3,g2)
    c: Coincident(g3,g2)
    c: Horizontal(g3)
    c: DistanceX(g3,g3) = 16
    c: Diameter(g2) = 16
    c: Coincident(g5,g4)
    c: Coincident(g5,g4)
    c: Horizontal(g5)
    c: DistanceX(g5,g5) = 15.6
    c: Diameter(g4) = 15.6002
    c: Coincident(g7,g6)
    c: Coincident(g7,g6)
    c: Horizontal(g7)
    c: DistanceX(g7,g7) = 15
FEATURE [PartDesign::Pocket] Pocket023  label="!!!!!!!!!!!!!!!!!!!!!!!!!!!!"
  Direction = (0,1,-2e-16)
  Length = 5
  Length2 = 5
  Profile = -> Sketch118
  ReferenceAxis = -> Sketch118 [N_Axis]
  Type = 0
FEATURE [Sketcher::SketchObject] Sketch119
  FullyConstrained = false
  MapMode = 5
  Placement = pos=(0,0,0) rot=(0.57735,-0.57735,-0.57735;2.0944rad)
  Support = -> [Pocket023]
  sketch-geometry (4):
    g0: LineSegment StartX=14.4002 StartY=0 StartZ=0 EndX=109.3 EndY=0 EndZ=0
    g1: LineSegment StartX=109.3 StartY=0 StartZ=0 EndX=109.3 EndY=4 EndZ=0
    g2: LineSegment StartX=109.3 StartY=4 StartZ=0 EndX=14.4002 EndY=4 EndZ=0
    g3: LineSegment StartX=14.4002 StartY=4 StartZ=0 EndX=14.4002 EndY=0 EndZ=0
  constraints (11):
    c: Coincident(g0,g1)
    c: Coincident(g1,g2)
    c: Coincident(g2,g3)
    c: Coincident(g3,g0)
    c: Horizontal(g0)
    c: Horizontal(g2)
    c: Vertical(g1)
    c: Vertical(g3)
    c: PointOnObject(g0,g-1)
    c: DistanceX(g2,g2) = 94.8998
    c: DistanceY(g1,g1) = 4
FEATURE [Part::Extrusion] Extrude044  label="Extrude074"
  Base = -> Sketch119
  Dir = (-1,0,0)
  DirMode = 2
  FaceMakerClass = Part::FaceMakerBullseye
  LengthFwd = 3
  LengthRev = 0
  Solid = true
  Symmetric = false
FEATURE [Sketcher::SketchObject] Sketch120
  FullyConstrained = false
  MapMode = 5
  Placement = pos=(84.2,0,0) rot=(0.57735,0.57735,0.57735;2.0944rad)
  Support = -> [Pocket023]
  sketch-geometry (4):
    g0: LineSegment StartX=-109.302 StartY=0 StartZ=0 EndX=-14.4 EndY=0 EndZ=0
    g1: LineSegment StartX=-14.4 StartY=0 StartZ=0 EndX=-14.4 EndY=4 EndZ=0
    g2: LineSegment StartX=-14.4 StartY=4 StartZ=0 EndX=-109.302 EndY=4 EndZ=0
    g3: LineSegment StartX=-109.302 StartY=4 StartZ=0 EndX=-109.302 EndY=0 EndZ=0
  constraints (11):
    c: Coincident(g0,g1)
    c: Coincident(g1,g2)
    c: Coincident(g2,g3)
    c: Coincident(g3,g0)
    c: Horizontal(g0)
    c: Horizontal(g2)
    c: Vertical(g1)
    c: Vertical(g3)
    c: PointOnObject(g0,g-1)
    c: DistanceX(g2,g2) = 94.9019
    c: DistanceY(g1,g1) = 4
FEATURE [Part::Extrusion] Extrude045  label="Extrude075"
  Base = -> Sketch120
  Dir = (1,0,0)
  DirMode = 2
  FaceMakerClass = Part::FaceMakerBullseye
  LengthFwd = 3
  LengthRev = 0
  Solid = true
  Symmetric = false
FEATURE [Sketcher::SketchObject] Sketch125
  FullyConstrained = false
  MapMode = 5
  Placement = pos=(0,-109.3,0) rot=(1,0,0;1.5708rad)
  Support = -> [Hole026]
  sketch-geometry (16):
    g0: LineSegment StartX=40.86 StartY=19.44 StartZ=0 EndX=31.16 EndY=19.44 EndZ=0
    g1: LineSegment StartX=43.5 StartY=19.44 StartZ=0 EndX=53.16 EndY=19.44 EndZ=0
    g2: LineSegment StartX=40.86 StartY=19.75 StartZ=0 EndX=43.5 EndY=19.75 EndZ=0
    g3: LineSegment StartX=43.5 StartY=19.75 StartZ=0 EndX=43.5 EndY=12.6 EndZ=0
    g4: LineSegment StartX=43.5 StartY=12.6 StartZ=0 EndX=40.86 EndY=12.6 EndZ=0
    g5: LineSegment StartX=40.86 StartY=12.6 StartZ=0 EndX=40.86 EndY=19.75 EndZ=0
    g6: LineSegment StartX=31.16 StartY=19.75 StartZ=0 EndX=33.8 EndY=19.75 EndZ=0
    g7: LineSegment StartX=33.8 StartY=19.75 StartZ=0 EndX=33.8 EndY=12.6 EndZ=0
    g8: LineSegment StartX=33.8 StartY=12.6 StartZ=0 EndX=31.16 EndY=12.6 EndZ=0
    g9: LineSegment StartX=31.16 StartY=12.6 StartZ=0 EndX=31.16 EndY=19.75 EndZ=0
    g10: LineSegment StartX=50.52 StartY=19.75 StartZ=0 EndX=53.16 EndY=19.75 EndZ=0
    g11: LineSegment StartX=53.16 StartY=19.75 StartZ=0 EndX=53.16 EndY=12.6 EndZ=0
    g12: LineSegment StartX=53.16 StartY=12.6 StartZ=0 EndX=50.52 EndY=12.6 EndZ=0
    g13: LineSegment StartX=50.52 StartY=12.6 StartZ=0 EndX=50.52 EndY=19.75 EndZ=0
    g14: LineSegment StartX=40.86 StartY=19.75 StartZ=0 EndX=31.16 EndY=19.75 EndZ=0
    g15: LineSegment StartX=43.5 StartY=19.75 StartZ=0 EndX=53.16 EndY=19.75 EndZ=0
  constraints (38):
    c: Horizontal(g0)
    c: DistanceX(g0,g0) = 9.7
    c: Horizontal(g1)
    c: DistanceX(g1,g1) = 9.66
    c: Coincident(g2,g3)
    c: Coincident(g3,g4)
    c: Coincident(g4,g5)
    c: Coincident(g5,g2)
    c: Horizontal(g2)
    c: Horizontal(g4)
    c: Vertical(g3)
    c: Vertical(g5)
    c: DistanceX(g2,g2) = 2.64
    c: DistanceY(g3,g3) = 7.15
    c: Coincident(g6,g7)
    c: Coincident(g7,g8)
    c: Coincident(g8,g9)
    c: Coincident(g9,g6)
    c: Horizontal(g6)
    c: Horizontal(g8)
    c: Vertical(g7)
    c: Vertical(g9)
    c: Coincident(g10,g11)
    c: Coincident(g11,g12)
    c: Coincident(g12,g13)
    c: Coincident(g13,g10)
    c: Horizontal(g10)
    c: Horizontal(g12)
    c: Vertical(g11)
    c: Vertical(g13)
    c: DistanceX(g6,g6) = 2.64
    c: DistanceX(g10,g10) = 2.64
    c: DistanceY(g9,g9) = 7.15
    c: DistanceY(g13,g13) = 7.15
    c: Coincident(g14,g2)
    c: Horizontal(g14)
    c: Coincident(g15,g2)
    c: Horizontal(g15)
FEATURE [PartDesign::Pocket] Pocket024
  BaseFeature = -> Hole026
  Direction = (0,1,-2e-16)
  Length = 5
  Length2 = 5
  Profile = -> Sketch125
  ReferenceAxis = -> Sketch125 [N_Axis]
  Type = 0
FEATURE [Sketcher::SketchObject] Sketch126
  FullyConstrained = false
  MapMode = 5
  Placement = pos=(-2.87e-14,-130.3,0) rot=(0,0.707107,0.707107;3.14159rad)
  Support = -> [Extrude043]
  sketch-geometry (4):
    g0: LineSegment StartX=10 StartY=5 StartZ=0 EndX=8 EndY=5 EndZ=0
    g1: LineSegment StartX=8 StartY=5 StartZ=0 EndX=8 EndY=2 EndZ=0
    g2: LineSegment StartX=8 StartY=2 StartZ=0 EndX=10 EndY=2 EndZ=0
    g3: LineSegment StartX=10 StartY=2 StartZ=0 EndX=10 EndY=5 EndZ=0
  constraints (10):
    c: Coincident(g0,g1)
    c: Coincident(g1,g2)
    c: Coincident(g2,g3)
    c: Coincident(g3,g0)
    c: Horizontal(g0)
    c: Horizontal(g2)
    c: Vertical(g1)
    c: Vertical(g3)
    c: DistanceX(g0,g0) = 2
    c: DistanceY(g1,g1) = 3
FEATURE [Part::Extrusion] Extrude048  label="Extrude077"
  Base = -> Sketch126
  Dir = (2e-16,1,-2e-16)
  DirMode = 2
  FaceMakerClass = Part::FaceMakerBullseye
  LengthFwd = 6.1
  LengthRev = 0
  Solid = true
  Symmetric = false
FEATURE [Sketcher::SketchObject] Sketch127
  FullyConstrained = false
  MapMode = 5
  Placement = pos=(-2.87e-14,-130.3,0) rot=(0,0.707107,0.707107;3.14159rad)
  Support = -> [Extrude042]
  sketch-geometry (4):
    g0: LineSegment StartX=-12 StartY=5 StartZ=0 EndX=-10 EndY=5 EndZ=0
    g1: LineSegment StartX=-10 StartY=5 StartZ=0 EndX=-10 EndY=2 EndZ=0
    g2: LineSegment StartX=-10 StartY=2 StartZ=0 EndX=-12 EndY=2 EndZ=0
    g3: LineSegment StartX=-12 StartY=2 StartZ=0 EndX=-12 EndY=5 EndZ=0
  constraints (10):
    c: Coincident(g0,g1)
    c: Coincident(g1,g2)
    c: Coincident(g2,g3)
    c: Coincident(g3,g0)
    c: Horizontal(g0)
    c: Horizontal(g2)
    c: Vertical(g1)
    c: Vertical(g3)
    c: DistanceX(g2,g2) = 2
    c: DistanceY(g1,g1) = 3
FEATURE [Part::Extrusion] Extrude049  label="Extrude078"
  Base = -> Sketch127
  Dir = (2e-16,1,-2e-16)
  DirMode = 2
  FaceMakerClass = Part::FaceMakerBullseye
  LengthFwd = 6.1
  LengthRev = 0
  Solid = true
  Symmetric = false
FEATURE [PartDesign::FeatureBase] BaseFeature015
  BaseFeature = -> Extrude049
FEATURE [Sketcher::SketchObject] Sketch128
  FullyConstrained = false
  MapMode = 5
  Placement = pos=(-10,2.2e-15,0) rot=(-0.57735,0.57735,0.57735;4.18879rad)
  Support = -> [Extrude048]
  sketch-geometry (1):
    g0: Circle CenterX=125.95 CenterY=3.5 CenterZ=0 NormalX=0 NormalY=0 NormalZ=1 AngleXU=0 Radius=0.75
  constraints (1):
    c: Diameter(g0) = 1.5
FEATURE [PartDesign::Hole] Hole027
  CustomThreadClearance = 0
  Depth = 2
  DepthType = 0
  Diameter = 1.5
  DrillForDepth = false
  DrillPoint = 1
  DrillPointAngle = 118
  HoleCutCountersinkAngle = 90
  HoleCutCustomValues = false
  HoleCutDepth = 0
  HoleCutDiameter = 6.1
  HoleCutType = 0
  ModelThread = false
  Profile = -> Sketch128
  Tapered = false
  TaperedAngle = 90
  ThreadClass = 0
  ThreadDepth = 2
  ThreadDepthType = 0
  ThreadDirection = 0
  ThreadFit = 0
  ThreadSize = 0
  ThreadType = 0
  Threaded = false
  UseCustomThreadClearance = false
FEATURE [Sketcher::SketchObject] Sketch129
  FullyConstrained = false
  MapMode = 5
  Placement = pos=(12,-2.6e-15,0) rot=(0.57735,0.57735,0.57735;2.0944rad)
  Support = -> [BaseFeature015]
  sketch-geometry (1):
    g0: Circle CenterX=-125.951 CenterY=3.5 CenterZ=0 NormalX=0 NormalY=0 NormalZ=1 AngleXU=0 Radius=0.75
  constraints (1):
    c: Diameter(g0) = 1.5
FEATURE [PartDesign::Hole] Hole028
  BaseFeature = -> BaseFeature015
  CustomThreadClearance = 0
  Depth = 14.3135
  DepthType = 0
  Diameter = 1.5
  DrillForDepth = false
  DrillPoint = 1
  DrillPointAngle = 118
  HoleCutCountersinkAngle = 90
  HoleCutCustomValues = false
  HoleCutDepth = 0
  HoleCutDiameter = 6.1
  HoleCutType = 0
  ModelThread = false
  Profile = -> Sketch129
  Tapered = false
  TaperedAngle = 90
  ThreadClass = 0
  ThreadDepth = 14.3135
  ThreadDepthType = 0
  ThreadDirection = 0
  ThreadFit = 0
  ThreadSize = 0
  ThreadType = 0
  Threaded = false
  UseCustomThreadClearance = false
FEATURE [PartDesign::Body] Body010  label="HANDLE LOCK"
  BaseFeature = -> Extrude049
  Group = -> [BaseFeature015,Sketch129,Hole028]
  Origin = -> Origin104
  Tip = -> Hole028
FEATURE [Sketcher::SketchObject] Sketch130
  FullyConstrained = false
  MapMode = 5
  Placement = pos=(-2.9e-14,-131.8,0) rot=(1,0,0;1.5708rad)
  Support = -> [Extrude042]
  sketch-geometry (8):
    g0: LineSegment StartX=-10 StartY=-7 StartZ=0 EndX=-8 EndY=-7 EndZ=0
    g1: LineSegment StartX=-8 StartY=-7 StartZ=0 EndX=-8 EndY=3 EndZ=0
    g2: LineSegment StartX=-8 StartY=3 StartZ=0 EndX=-10 EndY=3 EndZ=0
    g3: LineSegment StartX=-10 StartY=3 StartZ=0 EndX=-10 EndY=-7 EndZ=0
    g4: LineSegment StartX=10 StartY=3 StartZ=0 EndX=12 EndY=3 EndZ=0
    g5: LineSegment StartX=12 StartY=3 StartZ=0 EndX=12 EndY=-7 EndZ=0
    g6: LineSegment StartX=12 StartY=-7 StartZ=0 EndX=10 EndY=-7 EndZ=0
    g7: LineSegment StartX=10 StartY=-7 StartZ=0 EndX=10 EndY=3 EndZ=0
  constraints (20):
    c: Coincident(g0,g1)
    c: Coincident(g1,g2)
    c: Coincident(g2,g3)
    c: Coincident(g3,g0)
    c: Horizontal(g0)
    c: Horizontal(g2)
    c: Vertical(g1)
    c: Vertical(g3)
    c: Coincident(g4,g5)
    c: Coincident(g5,g6)
    c: Coincident(g6,g7)
    c: Coincident(g7,g4)
    c: Horizontal(g4)
    c: Horizontal(g6)
    c: Vertical(g5)
    c: Vertical(g7)
    c: DistanceX(g6,g6) = 2
    c: DistanceX(g0,g0) = 2
    c: DistanceY(g1,g1) = 10
    c: DistanceY(g7,g7) = 10
FEATURE [Part::Extrusion] Extrude050  label="Extrude079"
  Base = -> Sketch130
  Dir = (-2e-16,-1,2e-16)
  DirMode = 2
  FaceMakerClass = Part::FaceMakerBullseye
  LengthFwd = 1.5
  LengthRev = 0
  Solid = true
  Symmetric = false
FEATURE [App::Part] Part024  label="locking handle"
  Group = -> [Body010,Sketch090,Sketch113,Sketch116,Sketch115,Extrude041,Extrude043,Extrude042,Hole025,Sketch126,Sketch127,Sketch128,Extrude048,Extrude049,Hole027,Sketch130,Extrude050]
  Origin = -> Origin103
  Placement = pos=(41.16,20.68,14.44) rot=(0,0,1;0rad)
FEATURE [Sketcher::SketchObject] Sketch131
  FullyConstrained = false
  MapMode = 5
  Placement = pos=(0,-117,0) rot=(1,0,0;1.5708rad)
  Support = -> [BaseFeature016]
  sketch-geometry (20):
    g0: LineSegment StartX=-135.5 StartY=5.5 StartZ=0 EndX=-132.5 EndY=5.5 EndZ=0
    g1: LineSegment StartX=-132.5 StartY=5.5 StartZ=0 EndX=-132.5 EndY=1.5 EndZ=0
    g2: LineSegment StartX=-132.5 StartY=1.5 StartZ=0 EndX=-135.5 EndY=1.5 EndZ=0
    g3: LineSegment StartX=-135.5 StartY=1.5 StartZ=0 EndX=-135.5 EndY=5.5 EndZ=0
    g4: LineSegment StartX=-123 StartY=5 StartZ=0 EndX=-125 EndY=5 EndZ=0
    g5: LineSegment StartX=-125 StartY=5 StartZ=0 EndX=-125 EndY=2 EndZ=0
    g6: LineSegment StartX=-125 StartY=2 StartZ=0 EndX=-123 EndY=2 EndZ=0
    g7: LineSegment StartX=-123 StartY=2 StartZ=0 EndX=-123 EndY=5 EndZ=0
    g8: LineSegment StartX=-145 StartY=5 StartZ=0 EndX=-143 EndY=5 EndZ=0
    g9: LineSegment StartX=-143 StartY=5 StartZ=0 EndX=-143 EndY=2 EndZ=0
    g10: LineSegment StartX=-143 StartY=2 StartZ=0 EndX=-145 EndY=2 EndZ=0
    g11: LineSegment StartX=-145 StartY=2 StartZ=0 EndX=-145 EndY=5 EndZ=0
    g12: LineSegment StartX=-145.5 StartY=5.5 StartZ=0 EndX=-142.5 EndY=5.5 EndZ=0
    g13: LineSegment StartX=-142.5 StartY=5.5 StartZ=0 EndX=-142.5 EndY=1.5 EndZ=0
    g14: LineSegment StartX=-142.5 StartY=1.5 StartZ=0 EndX=-145.5 EndY=1.5 EndZ=0
    g15: LineSegment StartX=-145.5 StartY=1.5 StartZ=0 EndX=-145.5 EndY=5.5 EndZ=0
    g16: LineSegment StartX=-125.5 StartY=5.5 StartZ=0 EndX=-122.5 EndY=5.5 EndZ=0
    g17: LineSegment StartX=-122.5 StartY=5.5 StartZ=0 EndX=-122.5 EndY=1.5 EndZ=0
    g18: LineSegment StartX=-122.5 StartY=1.5 StartZ=0 EndX=-125.5 EndY=1.5 EndZ=0
    g19: LineSegment StartX=-125.5 StartY=1.5 StartZ=0 EndX=-125.5 EndY=5.5 EndZ=0
  constraints (46):
    c: Coincident(g0,g1)
    c: Coincident(g1,g2)
    c: Coincident(g2,g3)
    c: Coincident(g3,g0)
    c: Horizontal(g0)
    c: Horizontal(g2)
    c: Vertical(g1)
    c: Vertical(g3)
    c: Coincident(g4,g5)
    c: Coincident(g5,g6)
    c: Coincident(g6,g7)
    c: Coincident(g7,g4)
    c: Horizontal(g4)
    c: Horizontal(g6)
    c: Vertical(g5)
    c: Vertical(g7)
    c: Coincident(g8,g9)
    c: Coincident(g9,g10)
    c: Coincident(g10,g11)
    c: Coincident(g11,g8)
    c: Horizontal(g8)
    c: Horizontal(g10)
    c: Vertical(g9)
    c: Vertical(g11)
    c: Coincident(g12,g13)
    c: Coincident(g13,g14)
    c: Coincident(g14,g15)
    c: Coincident(g15,g12)
    c: Horizontal(g12)
    c: Horizontal(g14)
    c: Vertical(g13)
    c: Vertical(g15)
    c: Coincident(g16,g17)
    c: Coincident(g17,g18)
    c: Coincident(g18,g19)
    c: Coincident(g19,g16)
    c: Horizontal(g16)
    c: Horizontal(g18)
    c: Vertical(g17)
    c: Vertical(g19)
    c: DistanceY(g13,g13) = 4
    c: DistanceY(g1,g1) = 4
    c: DistanceY(g19,g19) = 4
    c: DistanceX(g12,g12) = 3
    c: DistanceX(g0,g0) = 3
    c: DistanceX(g16,g16) = 3
FEATURE [PartDesign::Pocket] Pocket025
  BaseFeature = -> BaseFeature016
  Direction = (0,1,-2e-16)
  Length = 4
  Length2 = 5
  Profile = -> Sketch131
  ReferenceAxis = -> Sketch131 [N_Axis]
  Type = 0
FEATURE [Sketcher::SketchObject] Sketch132
  FullyConstrained = false
  MapMode = 5
  Placement = pos=(-121,0,0) rot=(0.57735,0.57735,0.57735;2.0944rad)
  Support = -> [Pocket025]
  sketch-geometry (1):
    g0: Circle CenterX=-115.25 CenterY=3.5 CenterZ=0 NormalX=0 NormalY=0 NormalZ=1 AngleXU=0 Radius=0.75
  constraints (1):
    c: Diameter(g0) = 1.5
FEATURE [PartDesign::Hole] Hole029
  BaseFeature = -> Pocket025
  CustomThreadClearance = 0
  Depth = 24
  DepthType = 0
  Diameter = 1.5
  DrillForDepth = false
  DrillPoint = 0
  DrillPointAngle = 118
  HoleCutCountersinkAngle = 90
  HoleCutCustomValues = false
  HoleCutDepth = 0
  HoleCutDiameter = 6.1
  HoleCutType = 0
  ModelThread = false
  Profile = -> Sketch132
  Tapered = false
  TaperedAngle = 90
  ThreadClass = 0
  ThreadDepth = 24
  ThreadDepthType = 0
  ThreadDirection = 0
  ThreadFit = 0
  ThreadSize = 0
  ThreadType = 0
  Threaded = false
  UseCustomThreadClearance = false
FEATURE [PartDesign::Body] Body009  label="LOCK MECHANISM BODY"
  BaseFeature = -> Extrude047
  Group = -> [BaseFeature016,Sketch131,Pocket025,Sketch132,Hole029]
  Origin = -> Origin102
  Tip = -> Hole029
FEATURE [App::Part] Part023  label="locking mechanism"
  Group = -> [Body009,BaseFeature007,BaseFeature008,Sketch089,Extrude007,Sketch110,Sketch088,Sketch012,BaseFeature010,Pocket018,Sketch087,Sketch107,Sketch109,Extrude039,Extrude040,Pocket019,Hole018]
  Origin = -> Origin101
  Placement = pos=(176.16,9.99,14.45) rot=(0,0,1;0rad)
FEATURE [App::Part] Part028  label="Locking Components"
  Group = -> [Part023,Part024,Part025]
  Origin = -> Origin111
FEATURE [Sketcher::SketchObject] Sketch133
  FullyConstrained = false
  MapMode = 5
  Placement = pos=(0,-109.3,0) rot=(1,0,0;1.5708rad)
  Support = -> [Pocket024]
  sketch-geometry (8):
    g0: LineSegment StartX=7.1 StartY=19.01 StartZ=0 EndX=27.1 EndY=19.01 EndZ=0
    g1: LineSegment StartX=27.1 StartY=19.01 StartZ=0 EndX=27.1 EndY=4.01 EndZ=0
    g2: LineSegment StartX=27.1 StartY=4.01 StartZ=0 EndX=7.1 EndY=4.01 EndZ=0
    g3: LineSegment StartX=7.1 StartY=4.01 StartZ=0 EndX=7.1 EndY=19.01 EndZ=0
    g4: LineSegment StartX=57.1633 StartY=4 StartZ=0 EndX=77.1635 EndY=4 EndZ=0
    g5: LineSegment StartX=77.1635 StartY=4 StartZ=0 EndX=77.1635 EndY=19 EndZ=0
    g6: LineSegment StartX=77.1635 StartY=19 StartZ=0 EndX=57.1633 EndY=19 EndZ=0
    g7: LineSegment StartX=57.1633 StartY=19 StartZ=0 EndX=57.1633 EndY=4 EndZ=0
  constraints (20):
    c: Coincident(g0,g1)
    c: Coincident(g1,g2)
    c: Coincident(g2,g3)
    c: Coincident(g3,g0)
    c: Horizontal(g0)
    c: Horizontal(g2)
    c: Vertical(g1)
    c: Vertical(g3)
    c: Coincident(g4,g5)
    c: Coincident(g5,g6)
    c: Coincident(g6,g7)
    c: Coincident(g7,g4)
    c: Horizontal(g4)
    c: Horizontal(g6)
    c: Vertical(g5)
    c: Vertical(g7)
    c: DistanceY(g5,g5) = 15
    c: DistanceX(g6,g6) = 20.0002
    c: DistanceX(g0,g0) = 20
    c: DistanceY(g1,g1) = 15
FEATURE [PartDesign::Pocket] Pocket026
  BaseFeature = -> Pocket024
  Direction = (0,1,-2e-16)
  Length = 5
  Length2 = 5
  Profile = -> Sketch133
  ReferenceAxis = -> Sketch133 [N_Axis]
  Type = 0
FEATURE [PartDesign::Body] Body012  label="FRONT BODY"
  Group = -> [Sketch117,Hole026,Sketch125,Pocket024,Sketch133,Pocket026]
  Origin = -> Origin107
  Tip = -> Pocket026
FEATURE [App::Part] Part021  label="main enclosure"
  Group = -> [Body007,Extrude030,Extrude005,Sketch085,Sketch084,Body012,BaseFeature006,Sketch086,Sketch099,Extrude035,Sketch100,Sketch101,Hole021,Extrude036,Extrude033,BaseFeature009,Hole019,Sketch096,Sketch095,Sketch097,Sketch098,Sketch105,Extrude034,Hole020,Extrude038,Sketch106,Hole024,Extrude031,Sketch093,Sketch094,Pocket021,Sketch112,BaseFeature011,Extrude032,Pocket017,Sketch102,Hole022,Body008,Extrude029,+18 more]
  Origin = -> Origin097
FEATURE [App::Part] Part030  label="Battery"
  Group = -> [Part021,Part026,Part028,Part022,Part027,Sketch111,Extrude047]
  Origin = -> Origin114
  Placement = pos=(84.2,-17.7,19) rot=(0,-1,0;3.14159rad)
FEATURE [App::Part] Part020  label="Battery and Sleeve"
  Group = -> [Part030,Part043]
  Origin = -> Origin096
  Placement = pos=(182.9,199.9,7.2) rot=(0,0,1;0rad)
FEATURE [Sketcher::SketchObject] Sketch
  FullyConstrained = false
  MapMode = 5
  Support = -> [XY_Plane201]
  sketch-geometry (4):
    g0: LineSegment StartX=400 StartY=100 StartZ=0 EndX=490 EndY=100 EndZ=0
    g1: LineSegment StartX=490 StartY=100 StartZ=0 EndX=490 EndY=215 EndZ=0
    g2: LineSegment StartX=490 StartY=215 StartZ=0 EndX=400 EndY=215 EndZ=0
    g3: LineSegment StartX=400 StartY=215 StartZ=0 EndX=400 EndY=100 EndZ=0
  constraints (10):
    c: Coincident(g0,g1)
    c: Coincident(g1,g2)
    c: Coincident(g2,g3)
    c: Coincident(g3,g0)
    c: Horizontal(g0)
    c: Horizontal(g2)
    c: Vertical(g1)
    c: Vertical(g3)
    c: DistanceX(g2,g2) = 90
    c: DistanceY(g1,g1) = 115
FEATURE [PartDesign::Pad] Pad
  Direction = (0,0,1)
  Length = 24
  Length2 = 10
  Profile = -> Sketch
  ReferenceAxis = -> Sketch [N_Axis]
  Type = 0
FEATURE [Sketcher::SketchObject] Sketch137
  FullyConstrained = false
  MapMode = 5
  Placement = pos=(0,100,0) rot=(1,0,0;1.5708rad)
  Support = -> [Pad]
  sketch-geometry (4):
    g0: LineSegment StartX=402 StartY=22 StartZ=0 EndX=488 EndY=22 EndZ=0
    g1: LineSegment StartX=488 StartY=22 StartZ=0 EndX=488 EndY=2 EndZ=0
    g2: LineSegment StartX=488 StartY=2 StartZ=0 EndX=402 EndY=2 EndZ=0
    g3: LineSegment StartX=402 StartY=2 StartZ=0 EndX=402 EndY=22 EndZ=0
  constraints (8):
    c: Coincident(g0,g1)
    c: Coincident(g1,g2)
    c: Coincident(g2,g3)
    c: Coincident(g3,g0)
    c: Horizontal(g0)
    c: Horizontal(g2)
    c: Vertical(g1)
    c: Vertical(g3)
FEATURE [PartDesign::Pocket] Pocket
  BaseFeature = -> Pad
  Direction = (0,1,-2e-16)
  Length = 113
  Length2 = 5
  Profile = -> Sketch137
  ReferenceAxis = -> Sketch137 [N_Axis]
  Type = 0
FEATURE [PartDesign::Fillet] Fillet
  Base = -> Pocket [Edge14,Edge18,Edge17,Edge11]
  BaseFeature = -> Pocket
  Radius = 9
  SupportTransform = false
  UseAllEdges = false
FEATURE [PartDesign::Fillet] Fillet001
  Base = -> Fillet [Edge32,Edge18,Edge34,Edge15]
  BaseFeature = -> Fillet
  Radius = 5
  SupportTransform = false
  UseAllEdges = false
FEATURE [PartDesign::Fillet] Fillet002
  Base = -> Fillet001 [Edge27,Edge22,Edge17]
  BaseFeature = -> Fillet001
  Radius = 2
  SupportTransform = false
  UseAllEdges = false
FEATURE [Part::Feature] Part__Feature567  label="cell 1"
  Placement = pos=(12.04,-30.7,12.39) rot=(1,0,0;1.5708rad)
  shape: bbox 19.48 x 65 x 19.48 mm, 202 faces (baked)
FEATURE [Part::Feature] Part__Feature568  label="cell 2"
  Placement = pos=(32.02,-30.66,12.53) rot=(1,0,0;1.5708rad)
  shape: bbox 19.48 x 65 x 19.48 mm, 202 faces (baked)
FEATURE [Part::Feature] Part__Feature569  label="cell 3"
  Placement = pos=(51.96,-30.79,12.39) rot=(1,0,0;1.5708rad)
  shape: bbox 19.48 x 65 x 19.48 mm, 202 faces (baked)
FEATURE [Part::Feature] Part__Feature570  label="cell 4"
  Placement = pos=(71.99,-30.61,12.38) rot=(1,0,0;1.5708rad)
  shape: bbox 19.48 x 65 x 19.48 mm, 202 faces (baked)
FEATURE [Sketcher::SketchObject] Sketch138
  FullyConstrained = false
  MapMode = 5
  Placement = pos=(0,0,0) rot=(1,0,0;1.5708rad)
  Support = -> [XZ_Plane204]
  sketch-geometry (20):
    g0: LineSegment StartX=402 StartY=30 StartZ=0 EndX=412 EndY=30 EndZ=0
    g1: LineSegment StartX=488 StartY=30 StartZ=0 EndX=478 EndY=30 EndZ=0
    g2: ArcOfCircle CenterX=413 CenterY=12 CenterZ=0 NormalX=0 NormalY=0 NormalZ=1 AngleXU=0 Radius=9.5 StartAngle=1.5708 EndAngle=4.71239
    g3: LineSegment StartX=413 StartY=21.5 StartZ=0 EndX=477 EndY=21.5 EndZ=0
    g4: ArcOfCircle CenterX=477 CenterY=12 CenterZ=0 NormalX=0 NormalY=0 NormalZ=1 AngleXU=0 Radius=9.5 StartAngle=4.71239 EndAngle=7.85398
    g5: LineSegment StartX=477 StartY=2.49999 StartZ=0 EndX=413 EndY=2.49999 EndZ=0
    g6: LineSegment StartX=413 StartY=21.5 StartZ=0 EndX=413 EndY=2.49999 EndZ=0
    g7: LineSegment StartX=477 StartY=21.5 StartZ=0 EndX=477 EndY=2.49999 EndZ=0
    g8: LineSegment StartX=403.5 StartY=12 StartZ=0 EndX=414.972 EndY=12 EndZ=0
    g9: LineSegment StartX=414.972 StartY=12 StartZ=0 EndX=424.972 EndY=12 EndZ=0
    g10: LineSegment StartX=424.972 StartY=12 StartZ=0 EndX=434.972 EndY=12 EndZ=0
    g11: LineSegment StartX=434.972 StartY=12 StartZ=0 EndX=444.972 EndY=12 EndZ=0
    g12: LineSegment StartX=444.972 StartY=12 StartZ=0 EndX=454.972 EndY=12 EndZ=0
    g13: LineSegment StartX=454.972 StartY=12 StartZ=0 EndX=464.972 EndY=12 EndZ=0
    g14: LineSegment StartX=464.972 StartY=12 StartZ=0 EndX=474.983 EndY=12 EndZ=0
    g15: LineSegment StartX=474.983 StartY=12 StartZ=0 EndX=485.046 EndY=12 EndZ=0
    g16: Circle CenterX=414.972 CenterY=12 CenterZ=0 NormalX=0 NormalY=0 NormalZ=1 AngleXU=0 Radius=5
    g17: Circle CenterX=434.972 CenterY=12 CenterZ=0 NormalX=0 NormalY=0 NormalZ=1 AngleXU=0 Radius=5
    g18: Circle CenterX=454.972 CenterY=12 CenterZ=0 NormalX=0 NormalY=0 NormalZ=1 AngleXU=0 Radius=5
    g19: Circle CenterX=474.983 CenterY=12 CenterZ=0 NormalX=0 NormalY=0 NormalZ=1 AngleXU=0 Radius=5
  constraints (49):
    c: Horizontal(g0)
    c: Horizontal(g1)
    c: Radius(g2) = 9.5
    c: Coincident(g3,g2)
    c: Horizontal(g3)
    c: Coincident(g4,g3)
    c: Coincident(g5,g4)
    c: Coincident(g5,g2)
    c: Horizontal(g5)
    c: DistanceX(g3,g3) = 64
    c: DistanceX(g5,g5) = 64
    c: Radius(g4) = 9.5
    c: Coincident(g6,g2)
    c: Coincident(g6,g2)
    c: Vertical(g6)
    c: Coincident(g7,g3)
    c: Coincident(g7,g4)
    c: DistanceY(g6,g6) = 19
    c: PointOnObject(g8,g2)
    c: Horizontal(g8)
    c: Coincident(g9,g8)
    c: Horizontal(g9)
    c: Coincident(g10,g9)
    c: Horizontal(g10)
    c: Coincident(g11,g10)
    c: Horizontal(g11)
    c: Coincident(g12,g11)
    c: Horizontal(g12)
    c: Coincident(g13,g12)
    c: Horizontal(g13)
    c: Coincident(g14,g13)
    c: Horizontal(g14)
    c: Coincident(g15,g14)
    c: Horizontal(g15)
    c: Coincident(g16,g8)
    c: Coincident(g17,g10)
    c: Coincident(g18,g12)
    c: Coincident(g19,g14)
    c: Equal(g16,g17)
    c: Equal(g16,g18)
    c: Equal(g16,g19)
    c: Diameter(g16) = 10
    c: DistanceX(g15,g15) = 10.0633
    c: DistanceX(g14,g14) = 10.011
    c: DistanceX(g13,g13) = 10
    c: DistanceX(g12,g12) = 10
    c: DistanceX(g11,g11) = 10
    c: DistanceX(g10,g10) = 10
    c: DistanceX(g9,g9) = 10
FEATURE [PartDesign::Pad] Pad002
  Direction = (0,-1,2e-16)
  Length = 2
  Length2 = 10
  Placement = pos=(0,0,0) rot=(1,0,0;1.5708rad)
  Profile = -> Sketch138
  ReferenceAxis = -> Sketch138 [N_Axis]
  Type = 0
FEATURE [Sketcher::SketchObject] Sketch139
  FullyConstrained = false
  MapMode = 5
  Placement = pos=(0,-2,9e-16) rot=(1,0,0;1.5708rad)
  Support = -> [Pad002]
  sketch-geometry (12):
    g0: LineSegment StartX=477 StartY=2.5 StartZ=0 EndX=413 EndY=2.5 EndZ=0
    g1: LineSegment StartX=413 StartY=2.5 StartZ=0 EndX=413 EndY=3.5 EndZ=0
    g2: LineSegment StartX=413 StartY=3.5 StartZ=0 EndX=477 EndY=3.5 EndZ=0
    g3: LineSegment StartX=477 StartY=3.5 StartZ=0 EndX=477 EndY=2.5 EndZ=0
    g4: LineSegment StartX=403.569 StartY=13.1409 StartZ=0 EndX=404.6 EndY=13.1409 EndZ=0
    g5: LineSegment StartX=404.6 StartY=13.1409 StartZ=0 EndX=404.6 EndY=10.9 EndZ=0
    g6: LineSegment StartX=404.6 StartY=10.9 StartZ=0 EndX=403.569 EndY=10.9 EndZ=0
    g7: LineSegment StartX=403.569 StartY=10.9 StartZ=0 EndX=403.569 EndY=13.1409 EndZ=0
    g8: LineSegment StartX=486.429 StartY=13.1434 StartZ=0 EndX=485.4 EndY=13.1434 EndZ=0
    g9: LineSegment StartX=485.4 StartY=13.1434 StartZ=0 EndX=485.4 EndY=10.8554 EndZ=0
    g10: LineSegment StartX=485.4 StartY=10.8554 StartZ=0 EndX=486.429 EndY=10.8554 EndZ=0
    g11: LineSegment StartX=486.429 StartY=10.8554 StartZ=0 EndX=486.429 EndY=13.1434 EndZ=0
  constraints (30):
    c: Coincident(g0,g1)
    c: Coincident(g1,g2)
    c: Coincident(g2,g3)
    c: Coincident(g3,g0)
    c: Horizontal(g0)
    c: Horizontal(g2)
    c: Vertical(g1)
    c: Vertical(g3)
    c: Coincident(g4,g5)
    c: Coincident(g5,g6)
    c: Coincident(g6,g7)
    c: Coincident(g7,g4)
    c: Horizontal(g4)
    c: Horizontal(g6)
    c: Vertical(g5)
    c: Vertical(g7)
    c: Coincident(g8,g9)
    c: Coincident(g9,g10)
    c: Coincident(g10,g11)
    c: Coincident(g11,g8)
    c: Horizontal(g8)
    c: Horizontal(g10)
    c: Vertical(g9)
    c: Vertical(g11)
    c: DistanceX(g4,g4) = 1.03067
    c: DistanceX(g2,g2) = 64
    c: DistanceY(g1,g1) = 1
    c: DistanceY(g7,g7) = 2.2409
    c: DistanceY(g9,g9) = 2.288
    c: DistanceX(g8,g8) = 1.02889
FEATURE [PartDesign::Pad] Pad003
  BaseFeature = -> Pad002
  Direction = (0,-1,2e-16)
  Length = 65.5
  Length2 = 10
  Placement = pos=(0,0,0) rot=(1,0,0;1.5708rad)
  Profile = -> Sketch139
  ReferenceAxis = -> Sketch139 [N_Axis]
  Type = 0
FEATURE [Sketcher::SketchObject] Sketch140
  FullyConstrained = false
  MapMode = 5
  Placement = pos=(0,-67.5,3.05e-14) rot=(1,0,0;1.5708rad)
  Support = -> [Pad003]
  sketch-geometry (20):
    g0: LineSegment StartX=402 StartY=30 StartZ=0 EndX=412 EndY=30 EndZ=0
    g1: LineSegment StartX=488 StartY=30 StartZ=0 EndX=478 EndY=30 EndZ=0
    g2: ArcOfCircle CenterX=413 CenterY=12 CenterZ=0 NormalX=0 NormalY=0 NormalZ=1 AngleXU=0 Radius=9.5 StartAngle=1.5708 EndAngle=4.71239
    g3: LineSegment StartX=413 StartY=21.5 StartZ=0 EndX=477 EndY=21.5 EndZ=0
    g4: ArcOfCircle CenterX=477 CenterY=12 CenterZ=0 NormalX=0 NormalY=0 NormalZ=1 AngleXU=0 Radius=9.5 StartAngle=4.71239 EndAngle=7.85398
    g5: LineSegment StartX=477 StartY=2.49999 StartZ=0 EndX=413 EndY=2.49999 EndZ=0
    g6: LineSegment StartX=413 StartY=21.5 StartZ=0 EndX=413 EndY=2.49999 EndZ=0
    g7: LineSegment StartX=477 StartY=21.5 StartZ=0 EndX=477 EndY=2.49999 EndZ=0
    g8: LineSegment StartX=403.5 StartY=12 StartZ=0 EndX=414.972 EndY=12 EndZ=0
    g9: LineSegment StartX=414.972 StartY=12 StartZ=0 EndX=424.972 EndY=12 EndZ=0
    g10: LineSegment StartX=424.972 StartY=12 StartZ=0 EndX=434.972 EndY=12 EndZ=0
    g11: LineSegment StartX=434.972 StartY=12 StartZ=0 EndX=444.972 EndY=12 EndZ=0
    g12: LineSegment StartX=444.972 StartY=12 StartZ=0 EndX=454.972 EndY=12 EndZ=0
    g13: LineSegment StartX=454.972 StartY=12 StartZ=0 EndX=464.972 EndY=12 EndZ=0
    g14: LineSegment StartX=464.972 StartY=12 StartZ=0 EndX=474.983 EndY=12 EndZ=0
    g15: LineSegment StartX=474.983 StartY=12 StartZ=0 EndX=485.046 EndY=12 EndZ=0
    g16: Circle CenterX=414.972 CenterY=12 CenterZ=0 NormalX=0 NormalY=0 NormalZ=1 AngleXU=0 Radius=5
    g17: Circle CenterX=434.972 CenterY=12 CenterZ=0 NormalX=0 NormalY=0 NormalZ=1 AngleXU=0 Radius=5
    g18: Circle CenterX=454.972 CenterY=12 CenterZ=0 NormalX=0 NormalY=0 NormalZ=1 AngleXU=0 Radius=5
    g19: Circle CenterX=474.983 CenterY=12 CenterZ=0 NormalX=0 NormalY=0 NormalZ=1 AngleXU=0 Radius=5
  constraints (49):
    c: Horizontal(g0)
    c: Horizontal(g1)
    c: Radius(g2) = 9.5
    c: Coincident(g3,g2)
    c: Horizontal(g3)
    c: Coincident(g4,g3)
    c: Coincident(g5,g4)
    c: Coincident(g5,g2)
    c: Horizontal(g5)
    c: DistanceX(g3,g3) = 64
    c: DistanceX(g5,g5) = 64
    c: Radius(g4) = 9.5
    c: Coincident(g6,g2)
    c: Coincident(g6,g2)
    c: Vertical(g6)
    c: Coincident(g7,g3)
    c: Coincident(g7,g4)
    c: DistanceY(g6,g6) = 19
    c: PointOnObject(g8,g2)
    c: Horizontal(g8)
    c: Coincident(g9,g8)
    c: Horizontal(g9)
    c: Coincident(g10,g9)
    c: Horizontal(g10)
    c: Coincident(g11,g10)
    c: Horizontal(g11)
    c: Coincident(g12,g11)
    c: Horizontal(g12)
    c: Coincident(g13,g12)
    c: Horizontal(g13)
    c: Coincident(g14,g13)
    c: Horizontal(g14)
    c: Coincident(g15,g14)
    c: Horizontal(g15)
    c: Coincident(g16,g8)
    c: Coincident(g17,g10)
    c: Coincident(g18,g12)
    c: Coincident(g19,g14)
    c: Equal(g16,g17)
    c: Equal(g16,g18)
    c: Equal(g16,g19)
    c: Diameter(g16) = 10
    c: DistanceX(g15,g15) = 10.0633
    c: DistanceX(g14,g14) = 10.011
    c: DistanceX(g13,g13) = 10
    c: DistanceX(g12,g12) = 10
    c: DistanceX(g11,g11) = 10
    c: DistanceX(g10,g10) = 10
    c: DistanceX(g9,g9) = 10
FEATURE [PartDesign::Pad] Pad004
  BaseFeature = -> Pad003
  Direction = (0,-1,2e-16)
  Length = 2
  Length2 = 10
  Placement = pos=(0,0,0) rot=(1,0,0;1.5708rad)
  Profile = -> Sketch140
  ReferenceAxis = -> Sketch140 [N_Axis]
  Type = 0
FEATURE [Sketcher::SketchObject] Sketch141
  FullyConstrained = false
  MapMode = 5
  Placement = pos=(0,0,0) rot=(-1,0,0;1.5708rad)
  Support = -> [Pad004]
  sketch-geometry (4):
    g0: LineSegment StartX=477 StartY=-2.50537 StartZ=0 EndX=413 EndY=-2.50537 EndZ=0
    g1: LineSegment StartX=413 StartY=-2.50537 StartZ=0 EndX=413 EndY=-3.50537 EndZ=0
    g2: LineSegment StartX=413 StartY=-3.50537 StartZ=0 EndX=477 EndY=-3.50537 EndZ=0
    g3: LineSegment StartX=477 StartY=-3.50537 StartZ=0 EndX=477 EndY=-2.50537 EndZ=0
  constraints (10):
    c: Coincident(g0,g1)
    c: Coincident(g1,g2)
    c: Coincident(g2,g3)
    c: Coincident(g3,g0)
    c: Horizontal(g0)
    c: Horizontal(g2)
    c: Vertical(g1)
    c: Vertical(g3)
    c: DistanceX(g2,g2) = 64
    c: DistanceY(g1,g1) = 1
FEATURE [PartDesign::Pad] Pad005
  BaseFeature = -> Pad004
  Direction = (0,1,-2e-16)
  Length = 30
  Length2 = 10
  Placement = pos=(0,0,0) rot=(1,0,0;1.5708rad)
  Profile = -> Sketch141
  ReferenceAxis = -> Sketch141 [N_Axis]
  Type = 0
FEATURE [Sketcher::SketchObject] Sketch142
  FullyConstrained = false
  MapMode = 5
  Support = -> [XY_Plane205]
  sketch-geometry (4):
    g0: LineSegment StartX=-104.145 StartY=0 StartZ=0 EndX=-49.1448 EndY=0 EndZ=0
    g1: LineSegment StartX=-49.1448 StartY=0 StartZ=0 EndX=-49.1448 EndY=-18 EndZ=0
    g2: LineSegment StartX=-49.1448 StartY=-18 StartZ=0 EndX=-104.145 EndY=-18 EndZ=0
    g3: LineSegment StartX=-104.145 StartY=-18 StartZ=0 EndX=-104.145 EndY=0 EndZ=0
  constraints (11):
    c: Coincident(g0,g1)
    c: Coincident(g1,g2)
    c: Coincident(g2,g3)
    c: Coincident(g3,g0)
    c: Horizontal(g0)
    c: Horizontal(g2)
    c: Vertical(g1)
    c: Vertical(g3)
    c: PointOnObject(g0,g-1)
    c: DistanceX(g0,g0) = 55
    c: DistanceY(g1,g1) = 18
FEATURE [PartDesign::Pad] Pad006
  Direction = (0,0,1)
  Length = 3
  Length2 = 10
  Profile = -> Sketch142
  ReferenceAxis = -> Sketch142 [N_Axis]
  Type = 0
FEATURE [PartDesign::Fillet] Fillet003
  Base = -> Pad006 [Edge8,Edge1,Edge2,Edge5]
  BaseFeature = -> Pad006
  Radius = 8
  SupportTransform = false
  UseAllEdges = false
FEATURE [PartDesign::Body] Body016  label="BMS 4S board"
  Group = -> [Sketch142,Pad006,Fillet003]
  Origin = -> Origin205
  Placement = pos=(117.73,-4.35,3.61) rot=(0,0,1;0rad)
  Tip = -> Fillet003
FEATURE [App::Part] Part044  label="Batt Components"
  Group = -> [Part__Feature567,Part__Feature568,Part__Feature569,Part__Feature570,Body016]
  Origin = -> Origin203
  Placement = pos=(403,210.35,0) rot=(0,0,1;0rad)
FEATURE [Sketcher::SketchObject] Sketch143
  FullyConstrained = false
  MapMode = 5
  Placement = pos=(0,215,0) rot=(0,0.707107,0.707107;3.14159rad)
  Support = -> [Fillet002]
  sketch-geometry (9):
    g0: LineSegment StartX=-490 StartY=15 StartZ=0 EndX=-445 EndY=15 EndZ=0
    g1: LineSegment StartX=-445 StartY=24 StartZ=0 EndX=-445 EndY=12 EndZ=0
    g2: LineSegment StartX=-445 StartY=12 StartZ=0 EndX=-454.15 EndY=12 EndZ=0
    g3: LineSegment StartX=-454.15 StartY=12 StartZ=0 EndX=-454.15 EndY=14 EndZ=0
    g4: LineSegment StartX=-454.15 StartY=14 StartZ=0 EndX=-454.15 EndY=14.15 EndZ=0
    g5: LineSegment StartX=-454.15 StartY=14.15 StartZ=0 EndX=-435.85 EndY=14.15 EndZ=0
    g6: LineSegment StartX=-435.85 StartY=14.15 StartZ=0 EndX=-435.85 EndY=9.85 EndZ=0
    g7: LineSegment StartX=-435.85 StartY=9.85 StartZ=0 EndX=-454.15 EndY=9.85 EndZ=0
    g8: LineSegment StartX=-454.15 StartY=9.85 StartZ=0 EndX=-454.15 EndY=14.15 EndZ=0
  constraints (20):
    c: Horizontal(g0)
    c: Vertical(g1)
    c: Coincident(g2,g1)
    c: Horizontal(g2)
    c: Coincident(g3,g2)
    c: Vertical(g3)
    c: Coincident(g4,g3)
    c: Vertical(g4)
    c: Coincident(g5,g6)
    c: Coincident(g6,g7)
    c: Coincident(g7,g8)
    c: Coincident(g8,g5)
    c: Horizontal(g5)
    c: Horizontal(g7)
    c: Vertical(g6)
    c: Vertical(g8)
    c: Coincident(g5,g4)
    c: DistanceY(g6,g6) = 4.3
    c: DistanceX(g7,g7) = 18.3
    c: DistanceX(g2,g2) = 9.15
FEATURE [PartDesign::Pocket] Pocket027
  BaseFeature = -> Fillet002
  Direction = (0,-1,2e-16)
  Length = 2
  Length2 = 5
  Profile = -> Sketch143
  ReferenceAxis = -> Sketch143 [N_Axis]
  Type = 0
FEATURE [PartDesign::Fillet] Fillet004
  Base = -> Pocket027 [Edge72,Edge70,Edge74,Edge69]
  BaseFeature = -> Pocket027
  Radius = 2
  SupportTransform = false
  UseAllEdges = false
FEATURE [Sketcher::SketchObject] Sketch144
  FullyConstrained = false
  MapMode = 5
  Placement = pos=(0,2.3e-15,3.50537) rot=(0,0,1;3.14159rad)
  Support = -> [Pad005]
  sketch-geometry (5):
    g0: LineSegment StartX=-477 StartY=-30 StartZ=0 EndX=-445 EndY=-30 EndZ=0
    g1: LineSegment StartX=-459 StartY=-29 StartZ=0 EndX=-431 EndY=-29 EndZ=0
    g2: LineSegment StartX=-431 StartY=-29 StartZ=0 EndX=-431 EndY=-27 EndZ=0
    g3: LineSegment StartX=-431 StartY=-27 StartZ=0 EndX=-459 EndY=-27 EndZ=0
    g4: LineSegment StartX=-459 StartY=-27 StartZ=0 EndX=-459 EndY=-29 EndZ=0
  constraints (11):
    c: Horizontal(g0)
    c: Coincident(g1,g2)
    c: Coincident(g2,g3)
    c: Coincident(g3,g4)
    c: Coincident(g4,g1)
    c: Horizontal(g1)
    c: Horizontal(g3)
    c: Vertical(g2)
    c: Vertical(g4)
    c: DistanceX(g3,g3) = 28
    c: DistanceY(g2,g2) = 2
FEATURE [PartDesign::Pad] Pad007
  BaseFeature = -> Pad005
  Direction = (0,2e-16,1)
  Length = 15
  Length2 = 10
  Placement = pos=(0,0,0) rot=(1,0,0;1.5708rad)
  Profile = -> Sketch144
  ReferenceAxis = -> Sketch144 [N_Axis]
  Type = 0
FEATURE [Sketcher::SketchObject] Sketch146
  FullyConstrained = false
  MapMode = 5
  Placement = pos=(0,29,-1.92e-14) rot=(-1,0,0;1.5708rad)
  Support = -> [Pad007]
  sketch-geometry (4):
    g0: LineSegment StartX=435.85 StartY=-14.15 StartZ=0 EndX=454.15 EndY=-14.15 EndZ=0
    g1: LineSegment StartX=454.15 StartY=-14.15 StartZ=0 EndX=454.15 EndY=-9.85 EndZ=0
    g2: LineSegment StartX=454.15 StartY=-9.85 StartZ=0 EndX=435.85 EndY=-9.85 EndZ=0
    g3: LineSegment StartX=435.85 StartY=-9.85 StartZ=0 EndX=435.85 EndY=-14.15 EndZ=0
  constraints (10):
    c: Coincident(g0,g1)
    c: Coincident(g1,g2)
    c: Coincident(g2,g3)
    c: Coincident(g3,g0)
    c: Horizontal(g0)
    c: Horizontal(g2)
    c: Vertical(g1)
    c: Vertical(g3)
    c: DistanceY(g1,g1) = 4.3
    c: DistanceX(g2,g2) = 18.3
FEATURE [PartDesign::Pocket] Pocket028
  BaseFeature = -> Pad007
  Direction = (0,-1,2e-16)
  Length = 2
  Length2 = 5
  Placement = pos=(0,0,0) rot=(1,0,0;1.5708rad)
  Profile = -> Sketch146
  ReferenceAxis = -> Sketch146 [N_Axis]
  Type = 0
FEATURE [PartDesign::Fillet] Fillet005
  Base = -> Pocket028 [Edge111,Edge103]
  BaseFeature = -> Pocket028
  Placement = pos=(0,0,0) rot=(1,0,0;1.5708rad)
  Radius = 4
  SupportTransform = false
  UseAllEdges = false
FEATURE [PartDesign::Fillet] Fillet006
  Base = -> Fillet005 [Edge20,Edge3]
  BaseFeature = -> Fillet005
  Placement = pos=(0,0,0) rot=(1,0,0;1.5708rad)
  Radius = 6
  SupportTransform = false
  UseAllEdges = false
FEATURE [Sketcher::SketchObject] Sketch147
  FullyConstrained = false
  MapMode = 5
  Placement = pos=(0,29,-1.92e-14) rot=(-1,0,0;1.5708rad)
  Support = -> [Fillet006]
  sketch-geometry (5):
    g0: LineSegment StartX=454.15 StartY=-14.15 StartZ=0 EndX=454.15 EndY=-12 EndZ=0
    g1: LineSegment StartX=454.15 StartY=-12 StartZ=0 EndX=455.44 EndY=-12 EndZ=0
    g2: LineSegment StartX=455.44 StartY=-12 StartZ=0 EndX=434.56 EndY=-12 EndZ=0
    g3: Circle CenterX=434.56 CenterY=-12 CenterZ=0 NormalX=0 NormalY=0 NormalZ=1 AngleXU=0 Radius=0.65
    g4: Circle CenterX=455.44 CenterY=-12 CenterZ=0 NormalX=0 NormalY=0 NormalZ=1 AngleXU=0 Radius=0.65
  constraints (11):
    c: Vertical(g0)
    c: DistanceY(g0,g0) = 2.15
    c: Coincident(g1,g0)
    c: Horizontal(g1)
    c: DistanceX(g1,g1) = 1.29
    c: Horizontal(g2)
    c: DistanceX(g2,g2) = 20.88
    c: Coincident(g3,g2)
    c: Coincident(g4,g1)
    c: Equal(g4,g3)
    c: Diameter(g4) = 1.3
FEATURE [PartDesign::Pocket] Pocket029
  BaseFeature = -> Fillet006
  Direction = (0,-1,2e-16)
  Length = 2
  Length2 = 5
  Placement = pos=(0,0,0) rot=(1,0,0;1.5708rad)
  Profile = -> Sketch147
  ReferenceAxis = -> Sketch147 [N_Axis]
  Type = 0
FEATURE [Sketcher::SketchObject] Sketch148
  FullyConstrained = false
  MapMode = 5
  Placement = pos=(0,100,0) rot=(1,0,0;1.5708rad)
  Support = -> [Fillet004]
  sketch-geometry (15):
    g0: LineSegment StartX=402.038 StartY=20.61 StartZ=0 EndX=404.037 EndY=18.6111 EndZ=0
    g1: LineSegment StartX=404.037 StartY=18.6111 StartZ=0 EndX=486.037 EndY=18.6089 EndZ=0
    g2: LineSegment StartX=402.038 StartY=20.61 StartZ=0 EndX=488.038 EndY=20.61 EndZ=0
    g3: LineSegment StartX=486.037 StartY=18.6089 StartZ=0 EndX=488.038 EndY=20.61 EndZ=0
    g4: LineSegment StartX=486.037 StartY=18.6089 StartZ=0 EndX=487.037 EndY=19.6094 EndZ=0
    g5: Circle CenterX=487.037 CenterY=19.6094 CenterZ=0 NormalX=0 NormalY=0 NormalZ=1 AngleXU=0 Radius=1
    g6: LineSegment StartX=403.964 StartY=18.61 StartZ=0 EndX=402.972 EndY=19.6 EndZ=0
    g7: Circle CenterX=402.972 CenterY=19.6 CenterZ=0 NormalX=0 NormalY=0 NormalZ=1 AngleXU=0 Radius=1
    g8: LineSegment StartX=401.09 StartY=1.88287 StartZ=0 EndX=403.09 EndY=3.88372 EndZ=0
    g9: LineSegment StartX=403.09 StartY=3.88372 StartZ=0 EndX=486.91 EndY=3.88372 EndZ=0
    g10: LineSegment StartX=486.91 StartY=3.88372 StartZ=0 EndX=488.909 EndY=1.88258 EndZ=0
    g11: LineSegment StartX=488.909 StartY=1.88258 StartZ=0 EndX=487.91 EndY=2.88315 EndZ=0
    g12: LineSegment StartX=401.09 StartY=1.88287 StartZ=0 EndX=402.09 EndY=2.8833 EndZ=0
    g13: Circle CenterX=402.09 CenterY=2.8833 CenterZ=0 NormalX=0 NormalY=0 NormalZ=1 AngleXU=0 Radius=1
    g14: Circle CenterX=487.91 CenterY=2.88315 CenterZ=0 NormalX=0 NormalY=0 NormalZ=1 AngleXU=0 Radius=1
  constraints (30):
    c: Coincident(g1,g0)
    c: Coincident(g2,g0)
    c: Horizontal(g2)
    c: Coincident(g3,g1)
    c: Coincident(g3,g2)
    c: Distance(g3) = 2.83
    c: Angle(g0,g2) = 0.785398
    c: Angle(g2,g3) = 0.785398
    c: DistanceX(g2,g2) = 86
    c: DistanceX(g1,g1) = 82
    c: Coincident(g4,g1)
    c: PointOnObject(g4,g3)
    c: Distance(g4) = 1.415
    c: Coincident(g5,g4)
    c: Diameter(g5) = 2
    c: Coincident(g7,g6)
    c: Diameter(g7) = 2
    c: Coincident(g9,g8)
    c: Horizontal(g9)
    c: Coincident(g10,g9)
    c: Distance(g10) = 2.82855
    c: Coincident(g11,g10)
    c: PointOnObject(g11,g10)
    c: Distance(g8) = 2.82903
    c: Coincident(g12,g8)
    c: PointOnObject(g12,g8)
    c: Coincident(g13,g12)
    c: Coincident(g14,g11)
    c: Diameter(g14) = 2
    c: Diameter(g13) = 2
FEATURE [PartDesign::Body] Body  label="Battery Shell"
  Group = -> [Sketch,Pad,Sketch137,Pocket,Fillet,Fillet001,Fillet002,Sketch143,Pocket027,Fillet004,Sketch148]
  Origin = -> Origin201
  Placement = pos=(0,-1,0.25) rot=(0,0,1;0rad)
  Tip = -> Fillet004
FEATURE [Sketcher::SketchObject] Sketch149
  FullyConstrained = false
  MapMode = 5
  Placement = pos=(0,-69.5,1.54e-14) rot=(1,0,0;1.5708rad)
  Support = -> [Pocket029]
  sketch-geometry (16):
    g0: LineSegment StartX=486.43 StartY=13.1451 StartZ=0 EndX=483.4 EndY=13.1451 EndZ=0
    g1: LineSegment StartX=483.4 StartY=13.1451 StartZ=0 EndX=483.4 EndY=11.14 EndZ=0
    g2: LineSegment StartX=483.4 StartY=11.14 StartZ=0 EndX=486.43 EndY=11.14 EndZ=0
    g3: LineSegment StartX=486.43 StartY=11.14 StartZ=0 EndX=486.43 EndY=13.1451 EndZ=0
    g4: LineSegment StartX=448 StartY=3 StartZ=0 EndX=442 EndY=3 EndZ=0
    g5: LineSegment StartX=442 StartY=3 StartZ=0 EndX=442 EndY=6 EndZ=0
    g6: LineSegment StartX=442 StartY=6 StartZ=0 EndX=448 EndY=6 EndZ=0
    g7: LineSegment StartX=448 StartY=6 StartZ=0 EndX=448 EndY=3 EndZ=0
    g8: LineSegment StartX=403.57 StartY=13.145 StartZ=0 EndX=406.6 EndY=13.145 EndZ=0
    g9: LineSegment StartX=406.6 StartY=13.145 StartZ=0 EndX=406.6 EndY=11.1 EndZ=0
    g10: LineSegment StartX=406.6 StartY=11.1 StartZ=0 EndX=403.57 EndY=11.1 EndZ=0
    g11: LineSegment StartX=403.57 StartY=11.1 StartZ=0 EndX=403.57 EndY=13.145 EndZ=0
    g12: LineSegment StartX=442 StartY=21 StartZ=0 EndX=448 EndY=21 EndZ=0
    g13: LineSegment StartX=448 StartY=21 StartZ=0 EndX=448 EndY=18 EndZ=0
    g14: LineSegment StartX=448 StartY=18 StartZ=0 EndX=442 EndY=18 EndZ=0
    g15: LineSegment StartX=442 StartY=18 StartZ=0 EndX=442 EndY=21 EndZ=0
  constraints (40):
    c: Coincident(g0,g1)
    c: Coincident(g1,g2)
    c: Coincident(g2,g3)
    c: Coincident(g3,g0)
    c: Horizontal(g0)
    c: Horizontal(g2)
    c: Vertical(g1)
    c: Vertical(g3)
    c: Coincident(g4,g5)
    c: Coincident(g5,g6)
    c: Coincident(g6,g7)
    c: Coincident(g7,g4)
    c: Horizontal(g4)
    c: Horizontal(g6)
    c: Vertical(g5)
    c: Vertical(g7)
    c: Coincident(g8,g9)
    c: Coincident(g9,g10)
    c: Coincident(g10,g11)
    c: Coincident(g11,g8)
    c: Horizontal(g8)
    c: Horizontal(g10)
    c: Vertical(g9)
    c: Vertical(g11)
    c: Coincident(g12,g13)
    c: Coincident(g13,g14)
    c: Coincident(g14,g15)
    c: Coincident(g15,g12)
    c: Horizontal(g12)
    c: Horizontal(g14)
    c: Vertical(g13)
    c: Vertical(g15)
    c: DistanceY(g15,g15) = 3
    c: DistanceY(g5,g5) = 3
    c: DistanceY(g1,g1) = 2.00511
    c: DistanceY(g11,g11) = 2.04501
    c: DistanceX(g8,g8) = 3.03002
    c: DistanceX(g12,g12) = 6
    c: DistanceX(g6,g6) = 6
    c: DistanceX(g0,g0) = 3.03
FEATURE [PartDesign::Pad] Pad008
  BaseFeature = -> Pocket029
  Direction = (0,-1,2e-16)
  Length = 13.5
  Length2 = 10
  Placement = pos=(0,0,0) rot=(1,0,0;1.5708rad)
  Profile = -> Sketch149
  ReferenceAxis = -> Sketch149 [N_Axis]
  Type = 0
FEATURE [Sketcher::SketchObject] Sketch150
  FullyConstrained = false
  MapMode = 5
  Placement = pos=(0,-83,1.84e-14) rot=(1,0,0;1.5708rad)
  Support = -> [Pad008]
  sketch-geometry (5):
    g0: LineSegment StartX=409 StartY=24.25 StartZ=0 EndX=400 EndY=24.25 EndZ=0
    g1: LineSegment StartX=400 StartY=24.25 StartZ=0 EndX=490 EndY=24.25 EndZ=0
    g2: LineSegment StartX=490 StartY=24.25 StartZ=0 EndX=490 EndY=0.25 EndZ=0
    g3: LineSegment StartX=490 StartY=0.25 StartZ=0 EndX=400 EndY=0.25 EndZ=0
    g4: LineSegment StartX=400 StartY=0.25 StartZ=0 EndX=400 EndY=24.25 EndZ=0
  constraints (12):
    c: Horizontal(g0)
    c: Coincident(g1,g2)
    c: Coincident(g2,g3)
    c: Coincident(g3,g4)
    c: Coincident(g4,g1)
    c: Horizontal(g1)
    c: Horizontal(g3)
    c: Vertical(g2)
    c: Vertical(g4)
    c: Coincident(g1,g0)
    c: DistanceX(g3,g3) = 90
    c: DistanceY(g2,g2) = 24
FEATURE [PartDesign::Pad] Pad009
  BaseFeature = -> Pad008
  Direction = (0,-1,2e-16)
  Length = 2
  Length2 = 10
  Placement = pos=(0,0,0) rot=(1,0,0;1.5708rad)
  Profile = -> Sketch150
  ReferenceAxis = -> Sketch150 [N_Axis]
  Type = 0
FEATURE [PartDesign::Fillet] Fillet007
  Base = -> Pad009 [Edge2,Edge1]
  BaseFeature = -> Pad009
  Placement = pos=(0,0,0) rot=(1,0,0;1.5708rad)
  Radius = 9
  SupportTransform = false
  UseAllEdges = false
FEATURE [PartDesign::Fillet] Fillet008
  Base = -> Fillet007 [Edge34,Edge33]
  BaseFeature = -> Fillet007
  Placement = pos=(0,0,0) rot=(1,0,0;1.5708rad)
  Radius = 5
  SupportTransform = false
  UseAllEdges = false
FEATURE [Sketcher::SketchObject] Sketch151
  FullyConstrained = false
  MapMode = 5
  Support = -> [XY_Plane208]
  sketch-geometry (4):
    g0: LineSegment StartX=600 StartY=100 StartZ=0 EndX=780 EndY=100 EndZ=0
    g1: LineSegment StartX=780 StartY=100 StartZ=0 EndX=780 EndY=300 EndZ=0
    g2: LineSegment StartX=780 StartY=300 StartZ=0 EndX=600 EndY=300 EndZ=0
    g3: LineSegment StartX=600 StartY=300 StartZ=0 EndX=600 EndY=100 EndZ=0
  constraints (10):
    c: Coincident(g0,g1)
    c: Coincident(g1,g2)
    c: Coincident(g2,g3)
    c: Coincident(g3,g0)
    c: Horizontal(g0)
    c: Horizontal(g2)
    c: Vertical(g1)
    c: Vertical(g3)
    c: DistanceY(g3,g3) = 200
    c: DistanceX(g2,g2) = 180
FEATURE [PartDesign::Pad] Pad010
  Direction = (0,0,1)
  Length = 45
  Length2 = 10
  Profile = -> Sketch151
  ReferenceAxis = -> Sketch151 [N_Axis]
  Type = 0
FEATURE [Sketcher::SketchObject] Sketch152
  FullyConstrained = false
  MapMode = 5
  Placement = pos=(0,0,45) rot=(0,0,1;0rad)
  Support = -> [Pad010]
  sketch-geometry (4):
    g0: LineSegment StartX=746 StartY=100 StartZ=0 EndX=634 EndY=100 EndZ=0
    g1: LineSegment StartX=634 StartY=100 StartZ=0 EndX=634 EndY=233 EndZ=0
    g2: LineSegment StartX=634 StartY=233 StartZ=0 EndX=746 EndY=233 EndZ=0
    g3: LineSegment StartX=746 StartY=233 StartZ=0 EndX=746 EndY=100 EndZ=0
  constraints (10):
    c: Coincident(g0,g1)
    c: Coincident(g1,g2)
    c: Coincident(g2,g3)
    c: Coincident(g3,g0)
    c: Horizontal(g0)
    c: Horizontal(g2)
    c: Vertical(g1)
    c: Vertical(g3)
    c: DistanceX(g2,g2) = 112
    c: DistanceY(g1,g1) = 133
FEATURE [PartDesign::Pocket] Pocket030
  BaseFeature = -> Pad010
  Direction = (0,0,-1)
  Length = 3
  Length2 = 5
  Profile = -> Sketch152
  ReferenceAxis = -> Sketch152 [N_Axis]
  Type = 0
FEATURE [Sketcher::SketchObject] Sketch153
  FullyConstrained = false
  MapMode = 5
  Placement = pos=(0,0,42) rot=(0,0,1;0rad)
  Support = -> [Pocket030]
  sketch-geometry (4):
    g0: LineSegment StartX=642.5 StartY=99 StartZ=0 EndX=737.5 EndY=99 EndZ=0
    g1: LineSegment StartX=737.5 StartY=99 StartZ=0 EndX=737.5 EndY=233 EndZ=0
    g2: LineSegment StartX=737.5 StartY=233 StartZ=0 EndX=642.5 EndY=233 EndZ=0
    g3: LineSegment StartX=642.5 StartY=233 StartZ=0 EndX=642.5 EndY=99 EndZ=0
  constraints (10):
    c: Coincident(g0,g1)
    c: Coincident(g1,g2)
    c: Coincident(g2,g3)
    c: Coincident(g3,g0)
    c: Horizontal(g0)
    c: Horizontal(g2)
    c: Vertical(g1)
    c: Vertical(g3)
    c: DistanceX(g2,g2) = 95
    c: DistanceY(g3,g3) = 134
FEATURE [PartDesign::Pocket] Pocket031
  BaseFeature = -> Pocket030
  Direction = (0,0,-1)
  Length = 25
  Length2 = 5
  Profile = -> Sketch153
  ReferenceAxis = -> Sketch153 [N_Axis]
  Type = 0
FEATURE [PartDesign::Fillet] Fillet009
  Base = -> Pocket031 [Edge37,Edge23]
  BaseFeature = -> Pocket031
  Radius = 6.35
  SupportTransform = false
  UseAllEdges = false
FEATURE [PartDesign::Body] Body017  label="Body"
  Group = -> [Sketch151,Pad010,Sketch152,Pocket030,Sketch153,Pocket031,Fillet009]
  Origin = -> Origin208
  Tip = -> Fillet009
FEATURE [App::Part] Part045  label="Custom Battery Pocket "
  Group = -> [Body017]
  Origin = -> Origin206
  Placement = pos=(-43,-1,-17) rot=(0,0,1;0rad)
FEATURE [Sketcher::SketchObject] Sketch154
  FullyConstrained = false
  MapMode = 5
  Support = -> [XY_Plane210]
  sketch-geometry (4):
    g0: LineSegment StartX=600 StartY=100 StartZ=0 EndX=694.3 EndY=100 EndZ=0
    g1: LineSegment StartX=694.3 StartY=100 StartZ=0 EndX=694.3 EndY=233 EndZ=0
    g2: LineSegment StartX=694.3 StartY=233 StartZ=0 EndX=600 EndY=233 EndZ=0
    g3: LineSegment StartX=600 StartY=233 StartZ=0 EndX=600 EndY=100 EndZ=0
  constraints (10):
    c: Coincident(g0,g1)
    c: Coincident(g1,g2)
    c: Coincident(g2,g3)
    c: Coincident(g3,g0)
    c: Horizontal(g0)
    c: Horizontal(g2)
    c: Vertical(g1)
    c: Vertical(g3)
    c: DistanceX(g2,g2) = 94.3
    c: DistanceY(g3,g3) = 133
FEATURE [PartDesign::Pad] Pad011
  Direction = (0,0,1)
  Length = 28
  Length2 = 10
  Profile = -> Sketch154
  ReferenceAxis = -> Sketch154 [N_Axis]
  Type = 0
FEATURE [Sketcher::SketchObject] Sketch155
  FullyConstrained = false
  MapMode = 5
  Placement = pos=(0,100,0) rot=(1,0,0;1.5708rad)
  Support = -> [Pad011]
  sketch-geometry (4):
    g0: LineSegment StartX=601.65 StartY=1.5 StartZ=0 EndX=692.65 EndY=1.5 EndZ=0
    g1: LineSegment StartX=692.65 StartY=1.5 StartZ=0 EndX=692.65 EndY=26.5 EndZ=0
    g2: LineSegment StartX=692.65 StartY=26.5 StartZ=0 EndX=601.65 EndY=26.5 EndZ=0
    g3: LineSegment StartX=601.65 StartY=26.5 StartZ=0 EndX=601.65 EndY=1.5 EndZ=0
  constraints (10):
    c: Coincident(g0,g1)
    c: Coincident(g1,g2)
    c: Coincident(g2,g3)
    c: Coincident(g3,g0)
    c: Horizontal(g0)
    c: Horizontal(g2)
    c: Vertical(g1)
    c: Vertical(g3)
    c: DistanceX(g0,g0) = 91
    c: DistanceY(g1,g1) = 25
FEATURE [PartDesign::Pocket] Pocket032
  BaseFeature = -> Pad011
  Direction = (0,1,-2e-16)
  Length = 117.5
  Length2 = 5
  Profile = -> Sketch155
  ReferenceAxis = -> Sketch155 [N_Axis]
  Type = 0
FEATURE [PartDesign::Fillet] Fillet010
  Base = -> Pocket032 [Edge20,Edge17]
  BaseFeature = -> Pocket032
  Radius = 9
  SupportTransform = false
  UseAllEdges = false
FEATURE [PartDesign::Fillet] Fillet011
  Base = -> Fillet010 [Edge12,Edge16]
  BaseFeature = -> Fillet010
  Radius = 5
  SupportTransform = false
  UseAllEdges = false
FEATURE [Sketcher::SketchObject] Sketch156
  FullyConstrained = true
  MapMode = 5
  Placement = pos=(0,233,0) rot=(0,0.707107,0.707107;3.14159rad)
  Support = -> [Fillet011]
FEATURE [Sketcher::SketchObject] Sketch157
  FullyConstrained = false
  MapMode = 5
  Placement = pos=(694.3,0,0) rot=(0.57735,0.57735,0.57735;2.0944rad)
  Support = -> [Fillet011]
  sketch-geometry (4):
    g0: LineSegment StartX=100 StartY=28 StartZ=0 EndX=233 EndY=28 EndZ=0
    g1: LineSegment StartX=233 StartY=28 StartZ=0 EndX=233 EndY=25 EndZ=0
    g2: LineSegment StartX=233 StartY=25 StartZ=0 EndX=100 EndY=25 EndZ=0
    g3: LineSegment StartX=100 StartY=25 StartZ=0 EndX=100 EndY=28 EndZ=0
  constraints (10):
    c: Coincident(g0,g1)
    c: Coincident(g1,g2)
    c: Coincident(g2,g3)
    c: Coincident(g3,g0)
    c: Horizontal(g0)
    c: Horizontal(g2)
    c: Vertical(g1)
    c: Vertical(g3)
    c: DistanceX(g0,g0) = 133
    c: DistanceY(g1,g1) = 3
FEATURE [PartDesign::Pad] Pad012
  BaseFeature = -> Fillet011
  Direction = (1,0,0)
  Length = 8
  Length2 = 10
  Profile = -> Sketch157
  ReferenceAxis = -> Sketch157 [N_Axis]
  Type = 0
FEATURE [Sketcher::SketchObject] Sketch158
  FullyConstrained = false
  MapMode = 5
  Placement = pos=(600,0,0) rot=(0.57735,-0.57735,-0.57735;2.0944rad)
  Support = -> [Pad012]
  sketch-geometry (4):
    g0: LineSegment StartX=-233 StartY=28 StartZ=0 EndX=-100 EndY=28 EndZ=0
    g1: LineSegment StartX=-100 StartY=28 StartZ=0 EndX=-100 EndY=25 EndZ=0
    g2: LineSegment StartX=-100 StartY=25 StartZ=0 EndX=-233 EndY=25 EndZ=0
    g3: LineSegment StartX=-233 StartY=25 StartZ=0 EndX=-233 EndY=28 EndZ=0
  constraints (10):
    c: Coincident(g0,g1)
    c: Coincident(g1,g2)
    c: Coincident(g2,g3)
    c: Coincident(g3,g0)
    c: Horizontal(g0)
    c: Horizontal(g2)
    c: Vertical(g1)
    c: Vertical(g3)
    c: DistanceY(g3,g3) = 3
    c: DistanceX(g0,g0) = 133
FEATURE [PartDesign::Pad] Pad013
  BaseFeature = -> Pad012
  Direction = (-1,0,0)
  Length = 8
  Length2 = 10
  Profile = -> Sketch158
  ReferenceAxis = -> Sketch158 [N_Axis]
  Type = 0
FEATURE [PartDesign::Fillet] Fillet012
  Base = -> Pad013 [Edge34,Edge40,Edge60,Edge61]
  BaseFeature = -> Pad013
  Radius = 6.35
  SupportTransform = false
  UseAllEdges = false
FEATURE [Sketcher::SketchObject] Sketch159
  FullyConstrained = false
  MapMode = 5
  Placement = pos=(0,233,0) rot=(0,0.707107,0.707107;3.14159rad)
  Support = -> [Fillet012]
  sketch-geometry (4):
    g0: LineSegment StartX=-687 StartY=8 StartZ=0 EndX=-607.35 EndY=8 EndZ=0
    g1: LineSegment StartX=-607.35 StartY=8 StartZ=0 EndX=-607.35 EndY=20 EndZ=0
    g2: LineSegment StartX=-607.35 StartY=20 StartZ=0 EndX=-687 EndY=20 EndZ=0
    g3: LineSegment StartX=-687 StartY=20 StartZ=0 EndX=-687 EndY=8 EndZ=0
  constraints (10):
    c: Coincident(g0,g1)
    c: Coincident(g1,g2)
    c: Coincident(g2,g3)
    c: Coincident(g3,g0)
    c: Horizontal(g0)
    c: Horizontal(g2)
    c: Vertical(g1)
    c: Vertical(g3)
    c: DistanceX(g2,g2) = 79.65
    c: DistanceY(g3,g3) = 12
FEATURE [PartDesign::Pocket] Pocket033
  BaseFeature = -> Fillet012
  Direction = (0,-1,2e-16)
  Length = 14
  Length2 = 5
  Profile = -> Sketch159
  ReferenceAxis = -> Sketch159 [N_Axis]
  Type = 0
FEATURE [Sketcher::SketchObject] Sketch160
  FullyConstrained = false
  MapMode = 5
  Placement = pos=(0,219,0) rot=(0,0.707107,0.707107;3.14159rad)
  Support = -> [Pocket033]
  sketch-geometry (4):
    g0: LineSegment StartX=-656.35 StartY=16.2 StartZ=0 EndX=-638.05 EndY=16.2 EndZ=0
    g1: LineSegment StartX=-638.05 StartY=16.2 StartZ=0 EndX=-638.05 EndY=11.9 EndZ=0
    g2: LineSegment StartX=-638.05 StartY=11.9 StartZ=0 EndX=-656.35 EndY=11.9 EndZ=0
    g3: LineSegment StartX=-656.35 StartY=11.9 StartZ=0 EndX=-656.35 EndY=16.2 EndZ=0
  constraints (10):
    c: Coincident(g0,g1)
    c: Coincident(g1,g2)
    c: Coincident(g2,g3)
    c: Coincident(g3,g0)
    c: Horizontal(g0)
    c: Horizontal(g2)
    c: Vertical(g1)
    c: Vertical(g3)
    c: DistanceX(g0,g0) = 18.3
    c: DistanceY(g1,g1) = 4.3
FEATURE [PartDesign::Pocket] Pocket034
  BaseFeature = -> Pocket033
  Direction = (0,-1,2e-16)
  Length = 2
  Length2 = 5
  Profile = -> Sketch160
  ReferenceAxis = -> Sketch160 [N_Axis]
  Type = 0
FEATURE [PartDesign::Fillet] Fillet013
  Base = -> Pocket034 [Edge99,Edge100,Edge97,Edge98]
  BaseFeature = -> Pocket034
  Radius = 2
  SupportTransform = false
  UseAllEdges = false
FEATURE [Sketcher::SketchObject] Sketch161
  FullyConstrained = false
  MapMode = 5
  Placement = pos=(0,-83,9.2e-15) rot=(-1,0,0;1.5708rad)
  Support = -> [Fillet008]
  sketch-geometry (13):
    g0: LineSegment StartX=490 StartY=-15 StartZ=0 EndX=445 EndY=-15 EndZ=0
    g1: LineSegment StartX=448 StartY=-25 StartZ=0 EndX=454 EndY=-25 EndZ=0
    g2: LineSegment StartX=442 StartY=-25 StartZ=0 EndX=436 EndY=-25 EndZ=0
    g3: LineSegment StartX=454 StartY=-24.2576 StartZ=0 EndX=454 EndY=-21.2576 EndZ=0
    g4: LineSegment StartX=436 StartY=-24.2502 StartZ=0 EndX=436 EndY=-21.2502 EndZ=0
    g5: LineSegment StartX=454 StartY=-21.2576 StartZ=0 EndX=480 EndY=-21.2576 EndZ=0
    g6: LineSegment StartX=480 StartY=-21.2576 StartZ=0 EndX=480 EndY=-3.25759 EndZ=0
    g7: LineSegment StartX=480 StartY=-3.25759 StartZ=0 EndX=454 EndY=-3.25759 EndZ=0
    g8: LineSegment StartX=454 StartY=-3.25759 StartZ=0 EndX=454 EndY=-21.2576 EndZ=0
    g9: LineSegment StartX=436 StartY=-21.2502 StartZ=0 EndX=410 EndY=-21.2502 EndZ=0
    g10: LineSegment StartX=410 StartY=-21.2502 StartZ=0 EndX=410 EndY=-3.2502 EndZ=0
    g11: LineSegment StartX=410 StartY=-3.2502 StartZ=0 EndX=436 EndY=-3.2502 EndZ=0
    g12: LineSegment StartX=436 StartY=-3.2502 StartZ=0 EndX=436 EndY=-21.2502 EndZ=0
  constraints (32):
    c: Horizontal(g0)
    c: DistanceX(g0,g0) = 45
    c: Horizontal(g1)
    c: Horizontal(g2)
    c: DistanceX(g1,g1) = 6
    c: DistanceX(g2,g2) = 6
    c: Vertical(g3)
    c: DistanceY(g3,g3) = 3
    c: Vertical(g4)
    c: DistanceY(g4,g4) = 3
    c: Coincident(g5,g6)
    c: Coincident(g6,g7)
    c: Coincident(g7,g8)
    c: Coincident(g8,g5)
    c: Horizontal(g5)
    c: Horizontal(g7)
    c: Vertical(g6)
    c: Vertical(g8)
    c: Coincident(g5,g3)
    c: DistanceY(g8,g8) = 18
    c: DistanceX(g5,g5) = 26
    c: Coincident(g9,g10)
    c: Coincident(g10,g11)
    c: Coincident(g11,g12)
    c: Coincident(g12,g9)
    c: Horizontal(g9)
    c: Horizontal(g11)
    c: Vertical(g10)
    c: Vertical(g12)
    c: Coincident(g9,g4)
    c: DistanceY(g10,g10) = 18
    c: DistanceX(g9,g9) = 26
FEATURE [PartDesign::Pad] Pad014
  BaseFeature = -> Fillet008
  Direction = (0,1,-2e-16)
  Length = 9
  Length2 = 10
  Placement = pos=(0,0,0) rot=(1,0,0;1.5708rad)
  Profile = -> Sketch161
  ReferenceAxis = -> Sketch161 [N_Axis]
  Type = 0
FEATURE [Sketcher::SketchObject] Sketch162
  FullyConstrained = false
  MapMode = 5
  Placement = pos=(0,-85,1.89e-14) rot=(1,0,0;1.5708rad)
  Support = -> [Pad014]
  sketch-geometry (9):
    g0: LineSegment StartX=436 StartY=21.25 StartZ=0 EndX=454 EndY=21.25 EndZ=0
    g1: LineSegment StartX=434.5 StartY=4.79234 StartZ=0 EndX=411.5 EndY=4.79234 EndZ=0
    g2: LineSegment StartX=411.5 StartY=4.79234 StartZ=0 EndX=411.5 EndY=19.7 EndZ=0
    g3: LineSegment StartX=411.5 StartY=19.7 StartZ=0 EndX=434.5 EndY=19.7 EndZ=0
    g4: LineSegment StartX=434.5 StartY=19.7 StartZ=0 EndX=434.5 EndY=4.79234 EndZ=0
    g5: LineSegment StartX=478.5 StartY=4.75 StartZ=0 EndX=455.5 EndY=4.75 EndZ=0
    g6: LineSegment StartX=455.5 StartY=4.75 StartZ=0 EndX=455.5 EndY=19.7006 EndZ=0
    g7: LineSegment StartX=455.5 StartY=19.7006 StartZ=0 EndX=478.5 EndY=19.7006 EndZ=0
    g8: LineSegment StartX=478.5 StartY=19.7006 StartZ=0 EndX=478.5 EndY=4.75 EndZ=0
  constraints (22):
    c: Horizontal(g0)
    c: DistanceX(g0,g0) = 18
    c: Coincident(g1,g2)
    c: Coincident(g2,g3)
    c: Coincident(g3,g4)
    c: Coincident(g4,g1)
    c: Horizontal(g1)
    c: Horizontal(g3)
    c: Vertical(g2)
    c: Vertical(g4)
    c: DistanceX(g3,g3) = 23
    c: DistanceY(g2,g2) = 14.9077
    c: Coincident(g5,g6)
    c: Coincident(g6,g7)
    c: Coincident(g7,g8)
    c: Coincident(g8,g5)
    c: Horizontal(g5)
    c: Horizontal(g7)
    c: Vertical(g6)
    c: Vertical(g8)
    c: DistanceX(g7,g7) = 23
    c: DistanceY(g6,g6) = 14.9506
FEATURE [PartDesign::Pocket] Pocket035
  BaseFeature = -> Pad014
  Direction = (0,1,-2e-16)
  Length = 9.5
  Length2 = 5
  Placement = pos=(0,0,0) rot=(1,0,0;1.5708rad)
  Profile = -> Sketch162
  ReferenceAxis = -> Sketch162 [N_Axis]
  Type = 0
FEATURE [PartDesign::Fillet] Fillet014
  Base = -> Pocket035 [Edge120,Edge125]
  BaseFeature = -> Pocket035
  Placement = pos=(0,0,0) rot=(1,0,0;1.5708rad)
  Radius = 2
  SupportTransform = false
  UseAllEdges = false
FEATURE [PartDesign::Fillet] Fillet015
  Base = -> Fillet014 [Edge44,Edge1,Edge6,Edge49]
  BaseFeature = -> Fillet014
  Placement = pos=(0,0,0) rot=(1,0,0;1.5708rad)
  Radius = 2
  SupportTransform = false
  UseAllEdges = false
FEATURE [PartDesign::Fillet] Fillet016
  Base = -> Fillet015 [Edge3,Edge27,Edge28,Edge29,Edge26,Edge54,Edge61,Edge60,Edge59,Edge58]
  BaseFeature = -> Fillet015
  Placement = pos=(0,0,0) rot=(1,0,0;1.5708rad)
  Radius = 1
  SupportTransform = false
  UseAllEdges = false
FEATURE [Sketcher::SketchObject] Sketch163
  FullyConstrained = false
  MapMode = 5
  Placement = pos=(0,-85,2.83e-14) rot=(1,0,0;1.5708rad)
  Support = -> [Fillet016]
  sketch-geometry (4):
    g0: Circle CenterX=403 CenterY=19.8 CenterZ=0 NormalX=0 NormalY=0 NormalZ=1 AngleXU=0 Radius=0.75
    g1: Circle CenterX=487.04 CenterY=19.8 CenterZ=0 NormalX=0 NormalY=0 NormalZ=1 AngleXU=0 Radius=0.75
    g2: Circle CenterX=402.07 CenterY=3.2 CenterZ=0 NormalX=0 NormalY=0 NormalZ=1 AngleXU=0 Radius=0.75
    g3: Circle CenterX=488.1 CenterY=3.2 CenterZ=0 NormalX=0 NormalY=0 NormalZ=1 AngleXU=0 Radius=0.75
  constraints (4):
    c: Equal(g0,g1)
    c: Equal(g0,g3)
    c: Equal(g0,g2)
    c: Diameter(g0) = 1.5
FEATURE [PartDesign::Pocket] Pocket036
  BaseFeature = -> Fillet016
  Direction = (0,1,-4e-16)
  Length = 2
  Length2 = 5
  Placement = pos=(0,0,0) rot=(1,0,0;1.5708rad)
  Profile = -> Sketch163
  ReferenceAxis = -> Sketch163 [N_Axis]
  Type = 0
FEATURE [PartDesign::Body] Body015  label="Batt Component Insert"
  Group = -> [Sketch138,Pad002,Sketch139,Pad003,Sketch140,Pad004,Sketch141,Pad005,Sketch144,Pad007,Sketch146,Pocket028,Fillet005,Fillet006,Sketch147,Pocket029,Sketch149,Pad008,Sketch150,Pad009,Fillet007,Fillet008,Sketch161,Pad014,Sketch162,Pocket035,Fillet014,Fillet015,Fillet016,Sketch163,Pocket036]
  Origin = -> Origin204
  Placement = pos=(0,182,0) rot=(0,0,1;0rad)
  Tip = -> Pocket036
FEATURE [App::Part] Part  label="Battery V2"
  Group = -> [Body,Body015,Part044]
  Origin = -> Origin
  Placement = pos=(202.2,3,1.8) rot=(0,0,1;0rad)
FEATURE [Sketcher::SketchObject] Sketch164
  FullyConstrained = false
  MapMode = 5
  Placement = pos=(0,0,28) rot=(0,0,1;0rad)
  Support = -> [Fillet013]
  sketch-geometry (22):
    g0: LineSegment StartX=592 StartY=100 StartZ=0 EndX=596 EndY=100 EndZ=0
    g1: LineSegment StartX=596 StartY=100 StartZ=0 EndX=596 EndY=111.853 EndZ=0
    g2: LineSegment StartX=596 StartY=111.853 StartZ=0 EndX=596 EndY=139.169 EndZ=0
    g3: LineSegment StartX=596 StartY=139.169 StartZ=0 EndX=596 EndY=166 EndZ=0
    g4: LineSegment StartX=596 StartY=166 StartZ=0 EndX=596 EndY=193 EndZ=0
    g5: LineSegment StartX=596 StartY=193 StartZ=0 EndX=596 EndY=220 EndZ=0
    g6: LineSegment StartX=702.3 StartY=100 StartZ=0 EndX=698.3 EndY=100 EndZ=0
    g7: LineSegment StartX=596 StartY=220 StartZ=0 EndX=698.3 EndY=220 EndZ=0
    g8: LineSegment StartX=596 StartY=193 StartZ=0 EndX=698.3 EndY=193 EndZ=0
    g9: LineSegment StartX=596 StartY=166 StartZ=0 EndX=698.2 EndY=166 EndZ=0
    g10: LineSegment StartX=596 StartY=139.169 StartZ=0 EndX=698.3 EndY=139.169 EndZ=0
    g11: LineSegment StartX=596 StartY=111.853 StartZ=0 EndX=698.3 EndY=111.853 EndZ=0
    g12: Circle CenterX=698.3 CenterY=111.853 CenterZ=0 NormalX=0 NormalY=0 NormalZ=1 AngleXU=0 Radius=1.75
    g13: Circle CenterX=596 CenterY=111.853 CenterZ=0 NormalX=0 NormalY=0 NormalZ=1 AngleXU=0 Radius=1.75
    g14: Circle CenterX=596 CenterY=139.169 CenterZ=0 NormalX=0 NormalY=0 NormalZ=1 AngleXU=0 Radius=1.75
    g15: Circle CenterX=698.3 CenterY=139.169 CenterZ=0 NormalX=0 NormalY=0 NormalZ=1 AngleXU=0 Radius=1.75
    g16: Circle CenterX=698.3 CenterY=166 CenterZ=0 NormalX=0 NormalY=0 NormalZ=1 AngleXU=0 Radius=1.75
    g17: Circle CenterX=698.3 CenterY=193 CenterZ=0 NormalX=0 NormalY=0 NormalZ=1 AngleXU=0 Radius=1.75
    g18: Circle CenterX=698.3 CenterY=220 CenterZ=0 NormalX=0 NormalY=0 NormalZ=1 AngleXU=0 Radius=1.75
    g19: Circle CenterX=596 CenterY=220 CenterZ=0 NormalX=0 NormalY=0 NormalZ=1 AngleXU=0 Radius=1.75
    g20: Circle CenterX=596 CenterY=193 CenterZ=0 NormalX=0 NormalY=0 NormalZ=1 AngleXU=0 Radius=1.75
    g21: Circle CenterX=596 CenterY=166 CenterZ=0 NormalX=0 NormalY=0 NormalZ=1 AngleXU=0 Radius=1.75
  constraints (36):
    c: Horizontal(g0)
    c: Coincident(g1,g0)
    c: Vertical(g1)
    c: Coincident(g2,g1)
    c: Vertical(g2)
    c: Coincident(g3,g2)
    c: Vertical(g3)
    c: Coincident(g4,g3)
    c: Vertical(g4)
    c: Coincident(g5,g4)
    c: Vertical(g5)
    c: Horizontal(g6)
    c: Coincident(g7,g5)
    c: Horizontal(g7)
    c: Coincident(g8,g4)
    c: Horizontal(g8)
    c: Coincident(g9,g3)
    c: Horizontal(g9)
    c: Coincident(g10,g2)
    c: Horizontal(g10)
    c: Coincident(g11,g1)
    c: Horizontal(g11)
    c: Coincident(g12,g11)
    c: Coincident(g13,g1)
    c: Coincident(g14,g2)
    c: Coincident(g15,g10)
    c: Coincident(g17,g8)
    c: Coincident(g18,g7)
    c: Coincident(g19,g5)
    c: Coincident(g20,g4)
    c: Coincident(g21,g3)
    c: Equal(g15,g12)
    c: Equal(g15, g16-g21) x6
    c: Equal(g15,g14)
    c: Equal(g15,g13)
    c: Diameter(g15) = 3.5
FEATURE [PartDesign::Pocket] Pocket037
  BaseFeature = -> Fillet013
  Direction = (0,0,-1)
  Length = 3
  Length2 = 5
  Profile = -> Sketch164
  ReferenceAxis = -> Sketch164 [N_Axis]
  Type = 0
FEATURE [PartDesign::Fillet] Fillet017
  Base = -> Pocket037 [Edge101,Edge82]
  BaseFeature = -> Pocket037
  Radius = 3
  SupportTransform = false
  UseAllEdges = false
FEATURE [PartDesign::Fillet] Fillet018
  Base = -> Fillet017 [Edge101,Edge103,Edge99,Edge98]
  BaseFeature = -> Fillet017
  Radius = 1
  SupportTransform = false
  UseAllEdges = false
FEATURE [Sketcher::SketchObject] Sketch165
  FullyConstrained = false
  MapMode = 5
  Placement = pos=(0,3e-16,1.5) rot=(0,0,1;0rad)
  Support = -> [Fillet018]
  sketch-geometry (7):
    g0: LineSegment StartX=606.626 StartY=100 StartZ=0 EndX=647.682 EndY=100 EndZ=0
    g1: LineSegment StartX=647.682 StartY=100 StartZ=0 EndX=621.616 EndY=100 EndZ=0
    g2: LineSegment StartX=621.616 StartY=100 StartZ=0 EndX=621.616 EndY=112 EndZ=0
    g3: LineSegment StartX=647.682 StartY=100 StartZ=0 EndX=673.701 EndY=100 EndZ=0
    g4: LineSegment StartX=673.701 StartY=100 StartZ=0 EndX=673.701 EndY=112 EndZ=0
    g5: Circle CenterX=621.616 CenterY=112 CenterZ=0 NormalX=0 NormalY=0 NormalZ=1 AngleXU=0 Radius=1.5
    g6: Circle CenterX=673.701 CenterY=112 CenterZ=0 NormalX=0 NormalY=0 NormalZ=1 AngleXU=0 Radius=1.5
  constraints (13):
    c: Horizontal(g0)
    c: Coincident(g1,g0)
    c: PointOnObject(g1,g0)
    c: Coincident(g2,g1)
    c: Vertical(g2)
    c: Coincident(g3,g0)
    c: Horizontal(g3)
    c: Coincident(g4,g3)
    c: Vertical(g4)
    c: Coincident(g5,g2)
    c: Coincident(g6,g4)
    c: Equal(g5,g6)
    c: Diameter(g5) = 3
FEATURE [PartDesign::Hole] Hole
  BaseFeature = -> Fillet018
  CustomThreadClearance = 0
  Depth = 25
  DepthType = 0
  Diameter = 3.5
  DrillForDepth = false
  DrillPoint = 0
  DrillPointAngle = 118
  HoleCutCountersinkAngle = 90
  HoleCutCustomValues = false
  HoleCutDepth = 2.3
  HoleCutDiameter = 6.1
  HoleCutType = 2
  ModelThread = false
  Profile = -> Sketch165
  Tapered = false
  TaperedAngle = 90
  ThreadClass = 0
  ThreadDepth = 25
  ThreadDepthType = 0
  ThreadDirection = 0
  ThreadFit = 0
  ThreadSize = 0
  ThreadType = 0
  Threaded = false
  UseCustomThreadClearance = false
FEATURE [PartDesign::Body] Body018
  Group = -> [Sketch154,Pad011,Sketch155,Pocket032,Fillet010,Fillet011,Sketch156,Sketch157,Pad012,Sketch158,Pad013,Fillet012,Sketch159,Pocket033,Sketch160,Pocket034,Fillet013,Sketch164,Pocket037,Fillet017,Fillet018,Sketch165,Hole]
  Origin = -> Origin210
  Tip = -> Hole
FEATURE [App::Part] Part046  label="Battery Sleeve V2"
  Group = -> [Body018]
  Origin = -> Origin209
